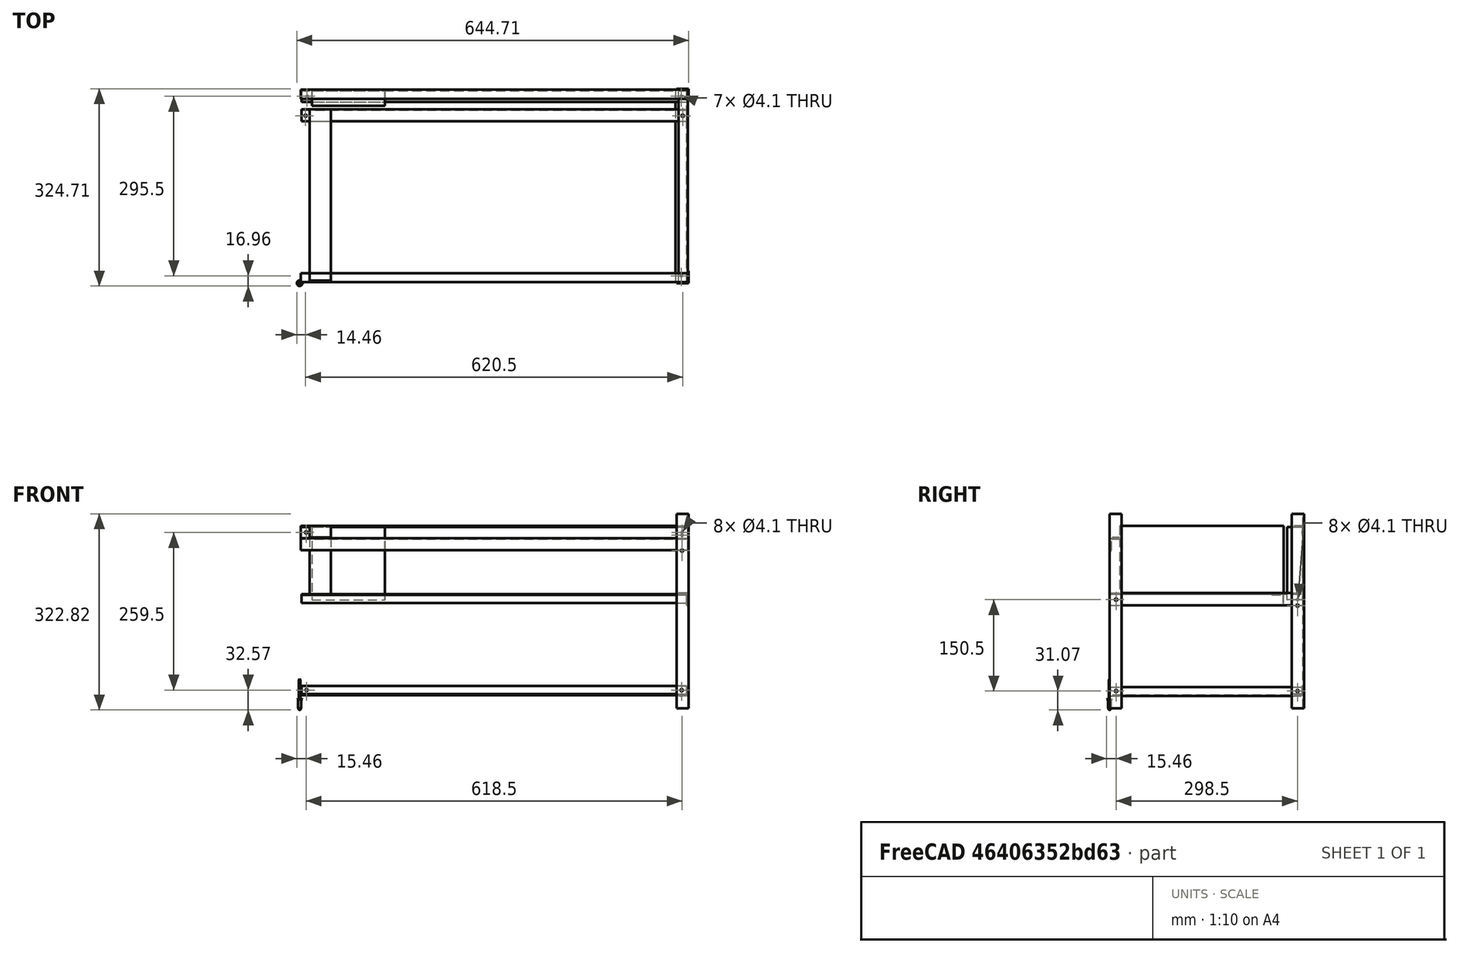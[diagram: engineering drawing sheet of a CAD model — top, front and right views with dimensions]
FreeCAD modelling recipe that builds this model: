
FCSTD DOCUMENT  (FreeCAD 0.17R13541 (Git))
Label: open_air_case_frame
License: All rights reserved
LicenseURL: http://en.wikipedia.org/wiki/All_rights_reserved
objects: TechDraw::DrawViewDimension×88, TechDraw::DrawViewPart×26, Sketcher::SketchObject×18, PartDesign::Hole×14, TechDraw::DrawViewAnnotation×14, TechDraw::DrawProjGroupItem×13, Part::Box×12, TechDraw::DrawSVGTemplate×10, TechDraw::DrawPage×10, PartDesign::FeatureBase×8, PartDesign::Mirrored×8, PartDesign::Body×8, TechDraw::DrawHatch×8, Part::Cut×6, TechDraw::DrawProjGroup×6, Part::Mirroring×5, App::DocumentObjectGroup×5, Part::Extrusion×4, App::FeaturePython×2, Spreadsheet::Sheet×1, +3 more types
note: 98 computed .brp shape members not serialized (recipe doc carries the construction recipe); baked Part::Feature solids carry a one-line shape summary decoded from their .brp

FEATURE [Part::Box] Box  label="Cube"
  AttacherType = Attacher::AttachEngine3D
  Height = 320
  Length = 20
  Width = 20
  expr: Length = Spreadsheet.bar_width
  expr: Width = Spreadsheet.bar_width
  expr: Height = parameters.height
FEATURE [Part::Box] Box001  label="Cut015"
  AttacherType = Attacher::AttachEngine3D
  Height = 320
  Length = 20
  Placement = pos=(1.5,1.5,0) rot=(0,0,1;0rad)
  Width = 20
  expr: Width = Spreadsheet.bar_width
  expr: Length = Spreadsheet.bar_width
  expr: Placement.Base.y = Spreadsheet.bar_thickness
  expr: Height = parameters.height
  expr: Placement.Base.x = Spreadsheet.bar_thickness
FEATURE [Part::Box] Box004  label="Cube002"
  AttacherType = Attacher::AttachEngine3D
  Height = 15
  Length = 20
  Width = 317
  expr: Width = parameters.depth - Spreadsheet.bar_thickness * 2
  expr: Height = Spreadsheet.bar_height
  expr: Length = Spreadsheet.bar_width
FEATURE [Part::Box] Box005  label="Cut016"
  AttacherType = Attacher::AttachEngine3D
  Height = 13.5
  Length = 20
  Placement = pos=(1.5,0,1.5) rot=(0,0,1;0rad)
  Width = 317
  expr: Length = Spreadsheet.bar_width
  expr: Width = parameters.depth - Spreadsheet.bar_thickness * 2
  expr: Placement.Base.z = Spreadsheet.bar_thickness
  expr: Height = Spreadsheet.bar_height - Spreadsheet.bar_thickness
  expr: Placement.Base.x = Spreadsheet.bar_thickness
FEATURE [Part::Box] Box006  label="Cube003"
  AttacherType = Attacher::AttachEngine3D
  Height = 20
  Length = 15
  Width = 317
  expr: Length = Spreadsheet.bar_height
  expr: Width = parameters.depth - Spreadsheet.bar_thickness * 2
  expr: Height = Spreadsheet.bar_width
FEATURE [Part::Box] Box007  label="Cut017"
  AttacherType = Attacher::AttachEngine3D
  Height = 20
  Length = 15
  Placement = pos=(1.5,0,-1.5) rot=(0,0,1;0rad)
  Width = 317
  expr: Placement.Base.z = Spreadsheet.bar_thickness * -1
  expr: Placement.Base.x = Spreadsheet.bar_thickness
  expr: Height = Spreadsheet.bar_width
  expr: Length = Spreadsheet.bar_height
  expr: Width = parameters.depth - Spreadsheet.bar_thickness * 2
FEATURE [Part::Box] Box008  label="Cube004"
  AttacherType = Attacher::AttachEngine3D
  Height = 320
  Length = 20
  Width = 20
  expr: Width = Spreadsheet.bar_width
  expr: Length = Spreadsheet.bar_width
  expr: Height = parameters.height
FEATURE [Part::Box] Box009  label="Cut018"
  AttacherType = Attacher::AttachEngine3D
  Height = 320
  Length = 20
  Placement = pos=(1.5,-1.5,0) rot=(0,0,1;0rad)
  Width = 20
  expr: Width = Spreadsheet.bar_width
  expr: Length = Spreadsheet.bar_width
  expr: Placement.Base.y = Spreadsheet.bar_thickness * -1
  expr: Height = parameters.height
  expr: Placement.Base.x = Spreadsheet.bar_thickness
FEATURE [Part::Box] Box010  label="reference_cube"
  AttacherType = Attacher::AttachEngine3D
  Height = 15
  Length = 634
  Placement = pos=(1.5,0,0) rot=(0,0,1;0rad)
  Width = 20
  expr: Width = Spreadsheet.bar_width
  expr: Length = parameters.width - Spreadsheet.bar_thickness * 4
  expr: Height = Spreadsheet.bar_height
  expr: Placement.Base.x = Spreadsheet.bar_thickness
FEATURE [Part::Box] Box011  label="reference_cube_cut"
  AttacherType = Attacher::AttachEngine3D
  Height = 15
  Length = 634
  Placement = pos=(1.5,1.5,1.5) rot=(0,0,1;0rad)
  Width = 20
  expr: Placement.Base.z = Spreadsheet.bar_thickness
  expr: Placement.Base.y = Spreadsheet.bar_thickness
  expr: Placement.Base.x = Spreadsheet.bar_thickness
  expr: Height = reference_cube.Height
  expr: Width = reference_cube.Width
  expr: Length = reference_cube.Length
FEATURE [Part::Cut] Cut005  label="lower_front_extrude"
  Base = -> Box010
  Placement = pos=(1.5,1.5,23) rot=(0,0,1;0rad)
  Tool = -> Box011
  expr: Placement.Base.z = Spreadsheet.bottom_empty_space + Spreadsheet.bar_thickness * 2
  expr: Placement.Base.y = Spreadsheet.bar_thickness
  expr: Placement.Base.x = Spreadsheet.bar_thickness
FEATURE [Part::Box] Box012  label="Cube007"
  AttacherType = Attacher::AttachEngine3D
  Height = 20
  Length = 637
  Placement = pos=(1.5,0,0) rot=(0,0,1;0rad)
  Width = 15
  expr: Length = parameters.width - Spreadsheet.bar_thickness * 2
  expr: Width = Spreadsheet.bar_height
  expr: Height = Spreadsheet.bar_width
  expr: Placement.Base.x = Spreadsheet.bar_thickness
FEATURE [Part::Box] Box013  label="Cube008"
  AttacherType = Attacher::AttachEngine3D
  Height = 20
  Length = 637
  Placement = pos=(1.5,1.5,-1.5) rot=(0,0,1;0rad)
  Width = 15
  expr: Placement.Base.z = Spreadsheet.bar_thickness * -1
  expr: Placement.Base.y = Spreadsheet.bar_thickness
  expr: Placement.Base.x = Spreadsheet.bar_thickness
  expr: Height = Spreadsheet.bar_width
  expr: Width = Spreadsheet.bar_height
  expr: Length = parameters.width - Spreadsheet.bar_thickness * 2
FEATURE [Part::Cut] Cut004  label="back_left_extrude"
  Base = -> Box008
  Placement = pos=(0,320,0) rot=(0,0,1;0rad)
  Tool = -> Box009
  expr: Placement.Base.y = parameters.depth
FEATURE [Part::Cut] Cut002  label="lower_left_extrude"
  Base = -> Box004
  Placement = pos=(1.5,1.5,21.5) rot=(0,0,1;0rad)
  Tool = -> Box005
  expr: Placement.Base.z = Spreadsheet.bottom_empty_space + Spreadsheet.bar_thickness
  expr: Placement.Base.y = Spreadsheet.bar_thickness
  expr: Placement.Base.x = Spreadsheet.bar_thickness
FEATURE [Part::Cut] Cut001  label="front_left_extrude"
  Base = -> Box
  Tool = -> Box001
FEATURE [Part::Cut] Cut  label="upper_front_extrude"
  Base = -> Box012
  Placement = pos=(0,1.5,250) rot=(0,0,1;0rad)
  Tool = -> Box013
  expr: Placement.Base.y = Spreadsheet.bar_thickness
FEATURE [Part::Cut] Cut013  label="upper_left_extrude"
  Base = -> Box006
  Placement = pos=(1.5,1.5,158) rot=(0,0,1;0rad)
  Tool = -> Box007
  expr: Placement.Base.y = Spreadsheet.bar_thickness
  expr: Placement.Base.x = Spreadsheet.bar_thickness
FEATURE [App::FeaturePython] Dimension  label="width"  # Draft dimension (typed FeaturePython)
  Dimline = (210,-128,0)
  Direction = (0,0,0)
  Distance = 640
  End = (640,0,0)
  Normal = (0,0,1)
  Start = (0,0,0)
FEATURE [App::FeaturePython] Dimension001  label="depth"  # Draft dimension (typed FeaturePython)
  Dimline = (720,145,0)
  Direction = (0,0,0)
  Distance = 320
  End = (640,320,0)
  Normal = (0,0,1)
  Start = (640,0,0)
FEATURE [PartDesign::FeatureBase] BaseFeature
  BaseFeature = -> Cut001
FEATURE [Sketcher::SketchObject] Sketch005
  AttachmentOffset = pos=(0,0,1.5) rot=(0,0,1;0rad)
  ExternalGeometry = -> [BaseFeature]
  MapMode = 5
  Placement = pos=(1.5,0,0) rot=(0.57735,0.57735,0.57735;2.0944rad)
  Support = -> [YZ_Plane]
  expr: Constraints[9] = 4.0999999999999996 / 2
  sketch-geometry (5):
    g0: LineSegment StartX=1.5 StartY=35 StartZ=0 EndX=20 EndY=35 EndZ=0
    g1: LineSegment StartX=20 StartY=35 StartZ=0 EndX=20 EndY=21.5 EndZ=0
    g2: LineSegment StartX=20 StartY=21.5 StartZ=0 EndX=1.5 EndY=21.5 EndZ=0
    g3: LineSegment StartX=1.5 StartY=21.5 StartZ=0 EndX=1.5 EndY=35 EndZ=0
    g4: Circle CenterX=10.75 CenterY=28.25 CenterZ=0 NormalX=0 NormalY=0 NormalZ=1 AngleXU=0 Radius=2.05
  constraints (14):
    c: Coincident(g0,g1)
    c: Coincident(g1,g2)
    c: Coincident(g2,g3)
    c: Coincident(g3,g0)
    c: Horizontal(g0)
    c: Horizontal(g2)
    c: Vertical(g1)
    c: Vertical(g3)
    c: Symmetric(g0,g1,g4)
    c: Radius(g4) = 2.05
    c: PointOnObject(g0,g-3)
    c: DistanceY(g-3,g1) = 21.5
    c: DistanceY(g1,g0) = 13.5
    c: PointOnObject(g0,g-4)
FEATURE [PartDesign::FeatureBase] BaseFeature001
  BaseFeature = -> Cut002
FEATURE [Sketcher::SketchObject] Sketch006
  AttachmentOffset = pos=(0,0,3) rot=(0,0,1;0rad)
  ExternalGeometry = -> [BaseFeature001]
  MapMode = 5
  Placement = pos=(3,0,0) rot=(0.57735,0.57735,0.57735;2.0944rad)
  Support = -> [YZ_Plane001]
  sketch-geometry (8):
    g0: LineSegment StartX=0 StartY=15 StartZ=0 EndX=18.5 EndY=15 EndZ=0
    g1: LineSegment StartX=18.5 StartY=15 StartZ=0 EndX=18.5 EndY=1.5 EndZ=0
    g2: LineSegment StartX=18.5 StartY=1.5 StartZ=0 EndX=0 EndY=1.5 EndZ=0
    g3: LineSegment StartX=0 StartY=1.5 StartZ=0 EndX=0 EndY=15 EndZ=0
    g4: Circle CenterX=9.25 CenterY=8.25 CenterZ=0 NormalX=0 NormalY=0 NormalZ=1 AngleXU=0 Radius=2.05
    g5: GeomPoint X=158.5 Y=15 Z=0
    g6: GeomPoint X=158.5 Y=1.5 Z=0
    g7: LineSegment [constr] StartX=158.5 StartY=15 StartZ=0 EndX=158.5 EndY=1.5 EndZ=0
  constraints (18):
    c: Coincident(g0,g1)
    c: Coincident(g1,g2)
    c: Coincident(g2,g3)
    c: Coincident(g3,g0)
    c: Horizontal(g0)
    c: Horizontal(g2)
    c: Vertical(g1)
    c: Vertical(g3)
    c: Symmetric(g0,g2,g4)
    c: PointOnObject(g0,g-3)
    c: PointOnObject(g1,g-4)
    c: PointOnObject(g0,g-2)
    c: DistanceX(g2,g1) = 18.5
    c: Radius(g4) = 2.05
    c: Symmetric(g0,g-3,g5)
    c: Symmetric(g-4,g2,g6)
    c: Coincident(g7,g5)
    c: Coincident(g7,g6)
FEATURE [PartDesign::Hole] Hole001
  BaseFeature = -> BaseFeature001
  Depth = 24
  DepthType = 1
  Diameter = 4.1
  DrillPoint = 1
  DrillPointAngle = 118
  HoleCutCountersinkAngle = 90
  HoleCutDepth = 0
  HoleCutDiameter = 0
  HoleCutType = 0
  ModelActualThread = false
  Profile = -> Sketch006
  Tapered = false
  TaperedAngle = 90
  ThreadAngle = 0
  ThreadClass = 0
  ThreadCutOffInner = 0
  ThreadCutOffOuter = 0
  ThreadDirection = 0
  ThreadFit = 0
  ThreadPitch = 0
  ThreadSize = 0
  ThreadType = 0
  Threaded = false
FEATURE [PartDesign::FeatureBase] BaseFeature002
  BaseFeature = -> Cut004
FEATURE [Sketcher::SketchObject] Sketch007
  AttachmentOffset = pos=(0,0,1.5) rot=(0,0,1;0rad)
  ExternalGeometry = -> [BaseFeature,BaseFeature002]
  MapMode = 5
  Placement = pos=(1.5,0,0) rot=(0.57735,0.57735,0.57735;2.0944rad)
  Support = -> [YZ_Plane002]
  expr: Constraints[9] = 4.0999999999999996 / 2
  sketch-geometry (10):
    g0: LineSegment StartX=0 StartY=35 StartZ=0 EndX=18.5 EndY=35 EndZ=0
    g1: LineSegment StartX=18.5 StartY=35 StartZ=0 EndX=18.5 EndY=21.5 EndZ=0
    g2: LineSegment StartX=18.5 StartY=21.5 StartZ=0 EndX=0 EndY=21.5 EndZ=0
    g3: LineSegment StartX=0 StartY=21.5 StartZ=0 EndX=0 EndY=35 EndZ=0
    g4: Circle CenterX=9.25 CenterY=28.25 CenterZ=0 NormalX=0 NormalY=0 NormalZ=1 AngleXU=0 Radius=2.05
    g5: Circle CenterX=9.25 CenterY=168.75 CenterZ=0 NormalX=0 NormalY=0 NormalZ=1 AngleXU=0 Radius=2.05
    g6: LineSegment StartX=-2e-11 StartY=178 StartZ=0 EndX=18.5 EndY=178 EndZ=0
    g7: LineSegment StartX=18.5 StartY=178 StartZ=0 EndX=18.5 EndY=159.5 EndZ=0
    g8: LineSegment StartX=18.5 StartY=159.5 StartZ=0 EndX=-2e-11 EndY=159.5 EndZ=0
    g9: LineSegment StartX=-2e-11 StartY=159.5 StartZ=0 EndX=-2e-11 EndY=178 EndZ=0
  constraints (28):
    c: Coincident(g0,g1)
    c: Coincident(g1,g2)
    c: Coincident(g2,g3)
    c: Coincident(g3,g0)
    c: Horizontal(g0)
    c: Horizontal(g2)
    c: Vertical(g1)
    c: Vertical(g3)
    c: Symmetric(g0,g1,g4)
    c: Radius(g4) = 2.05
    c: DistanceY(g-3,g1) = 21.5
    c: DistanceY(g1,g0) = 13.5
    c: PointOnObject(g0,g-4)
    c: PointOnObject(g0,g-2)
    c: Coincident(g6,g7)
    c: Coincident(g7,g8)
    c: Coincident(g8,g9)
    c: Coincident(g9,g6)
    c: Horizontal(g6)
    c: Horizontal(g8)
    c: Vertical(g7)
    c: Vertical(g9)
    c: Symmetric(g6,g7,g5)
    c: PointOnObject(g6,g-5)
    c: PointOnObject(g7,g-4)
    c: Equal(g6,g9)
    c: Radius(g5) = 2.05
    c: DistanceY(g-1,g8) = 159.5
FEATURE [PartDesign::Hole] Hole  label="Front Left Bottom Hole"
  BaseFeature = -> BaseFeature
  Depth = 25
  DepthType = 1
  Diameter = 4.1
  DrillPoint = 1
  DrillPointAngle = 118
  HoleCutCountersinkAngle = 90
  HoleCutDepth = 0
  HoleCutDiameter = 0
  HoleCutType = 0
  ModelActualThread = false
  Profile = -> Sketch005
  Tapered = false
  TaperedAngle = 90
  ThreadAngle = 0
  ThreadClass = 0
  ThreadCutOffInner = 0
  ThreadCutOffOuter = 0
  ThreadDirection = 0
  ThreadFit = 0
  ThreadPitch = 0
  ThreadSize = 0
  ThreadType = 0
  Threaded = false
FEATURE [PartDesign::Hole] Hole002
  BaseFeature = -> BaseFeature002
  Depth = 25
  DepthType = 1
  Diameter = 4.1
  DrillPoint = 1
  DrillPointAngle = 118
  HoleCutCountersinkAngle = 90
  HoleCutDepth = 0
  HoleCutDiameter = 0
  HoleCutType = 0
  ModelActualThread = false
  Profile = -> Sketch007
  Tapered = false
  TaperedAngle = 90
  ThreadAngle = 0
  ThreadClass = 0
  ThreadCutOffInner = 0
  ThreadCutOffOuter = 0
  ThreadDirection = 0
  ThreadFit = 0
  ThreadPitch = 0
  ThreadSize = 0
  ThreadType = 0
  Threaded = false
FEATURE [PartDesign::Mirrored] Mirrored
  BaseFeature = -> Hole001
  MirrorPlane = -> Sketch006 [Axis0]
  Originals = -> [Hole001]
FEATURE [PartDesign::FeatureBase] BaseFeature003
  BaseFeature = -> Cut005
FEATURE [Sketcher::SketchObject] Sketch008  label="Bottom"
  AttachmentOffset = pos=(0,0,1.5) rot=(0,0,1;0rad)
  ExternalGeometry = -> [Mirrored]
  MapMode = 5
  Placement = pos=(0,0,1.5) rot=(0,0,1;0rad)
  Support = -> [XY_Plane001]
  sketch-geometry (8):
    g0: Circle CenterX=10.75 CenterY=10.75 CenterZ=0 NormalX=0 NormalY=0 NormalZ=1 AngleXU=0 Radius=2.05
    g1: LineSegment StartX=1.5 StartY=20 StartZ=0 EndX=20 EndY=20 EndZ=0
    g2: LineSegment StartX=20 StartY=20 StartZ=0 EndX=20 EndY=1.5 EndZ=0
    g3: LineSegment StartX=20 StartY=1.5 StartZ=0 EndX=1.5 EndY=1.5 EndZ=0
    g4: LineSegment StartX=1.5 StartY=1.5 StartZ=0 EndX=1.5 EndY=20 EndZ=0
    g5: GeomPoint X=20 Y=158.5 Z=0
    g6: GeomPoint X=1.5 Y=158.5 Z=0
    g7: LineSegment [constr] StartX=20 StartY=158.5 StartZ=0 EndX=1.5 EndY=158.5 EndZ=0
  constraints (17):
    c: Coincident(g1,g2)
    c: Coincident(g2,g3)
    c: Coincident(g3,g4)
    c: Coincident(g4,g1)
    c: Horizontal(g1)
    c: Horizontal(g3)
    c: Vertical(g2)
    c: Vertical(g4)
    c: Symmetric(g1,g3,g0)
    c: Symmetric(g2,g1,g0)
    c: DistanceY(g-1,g2) = 1.5
    c: DistanceY(g2,g1) = 18.5
    c: Radius(g0) = 2.05
    c: Coincident(g7,g5)
    c: Coincident(g7,g6)
    c: Symmetric(g-4,g-4,g5)
    c: Symmetric(g-3,g-3,g6)
FEATURE [PartDesign::Hole] Hole003
  BaseFeature = -> Mirrored
  Depth = 25
  DepthType = 1
  Diameter = 4.1
  DrillPoint = 1
  DrillPointAngle = 118
  HoleCutCountersinkAngle = 90
  HoleCutDepth = 0
  HoleCutDiameter = 0
  HoleCutType = 0
  ModelActualThread = false
  Profile = -> Sketch008
  Tapered = false
  TaperedAngle = 90
  ThreadAngle = 0
  ThreadClass = 0
  ThreadCutOffInner = 0
  ThreadCutOffOuter = 0
  ThreadDirection = 0
  ThreadFit = 0
  ThreadPitch = 0
  ThreadSize = 0
  ThreadType = 0
  Threaded = false
FEATURE [PartDesign::Mirrored] Mirrored001
  BaseFeature = -> Hole003
  MirrorPlane = -> Sketch008 [Axis0]
  Originals = -> [Hole003]
FEATURE [PartDesign::Body] Body001  label="side_bottom_body"
  BaseFeature = -> Cut002
  Group = -> [BaseFeature001,Sketch006,Hole001,Mirrored,Sketch008,Hole003,Mirrored001]
  Origin = -> Origin001
  Placement = pos=(1.5,1.5,20) rot=(0,0,1;0rad)
  Tip = -> Mirrored001
  expr: Placement.Base.z = Spreadsheet.bar_width
  expr: Placement.Base.y = Spreadsheet.bar_thickness
  expr: Placement.Base.x = Spreadsheet.bar_thickness
FEATURE [Sketcher::SketchObject] Sketch009
  AttachmentOffset = pos=(0,0,1.5) rot=(0,0,1;0rad)
  ExternalGeometry = -> [BaseFeature003]
  MapMode = 5
  Placement = pos=(0,0,1.5) rot=(0,0,1;0rad)
  Support = -> [XY_Plane003]
  sketch-geometry (8):
    g0: Circle CenterX=10.75 CenterY=10.75 CenterZ=0 NormalX=0 NormalY=0 NormalZ=1 AngleXU=0 Radius=2.05
    g1: LineSegment StartX=1.5 StartY=20 StartZ=0 EndX=20 EndY=20 EndZ=0
    g2: LineSegment StartX=20 StartY=20 StartZ=0 EndX=20 EndY=1.5 EndZ=0
    g3: LineSegment StartX=20 StartY=1.5 StartZ=0 EndX=1.5 EndY=1.5 EndZ=0
    g4: LineSegment StartX=1.5 StartY=1.5 StartZ=0 EndX=1.5 EndY=20 EndZ=0
    g5: GeomPoint X=318.5 Y=20 Z=0
    g6: GeomPoint X=318.5 Y=0.75 Z=0
    g7: LineSegment [constr] StartX=318.5 StartY=20 StartZ=0 EndX=318.5 EndY=0.75 EndZ=0
  constraints (19):
    c: Coincident(g1,g2)
    c: Coincident(g2,g3)
    c: Coincident(g3,g4)
    c: Coincident(g4,g1)
    c: Horizontal(g1)
    c: Horizontal(g3)
    c: Vertical(g2)
    c: Vertical(g4)
    c: Symmetric(g1,g3,g0)
    c: Symmetric(g1,g2,g0)
    c: PointOnObject(g1,g-3)
    c: PointOnObject(g3,g-4)
    c: DistanceX(g-1,g3) = 1.5
    c: DistanceX(g3,g2) = 18.5
    c: Radius(g0) = 2.05
    c: Symmetric(g-3,g1,g5)
    c: Coincident(g7,g5)
    c: Coincident(g7,g6)
    c: Symmetric(g-5,g3,g6)
FEATURE [PartDesign::Hole] Hole004
  BaseFeature = -> BaseFeature003
  Depth = 25
  DepthType = 1
  Diameter = 4.1
  DrillPoint = 1
  DrillPointAngle = 118
  HoleCutCountersinkAngle = 90
  HoleCutDepth = 0
  HoleCutDiameter = 0
  HoleCutType = 0
  ModelActualThread = false
  Profile = -> Sketch009
  Tapered = false
  TaperedAngle = 90
  ThreadAngle = 0
  ThreadClass = 0
  ThreadCutOffInner = 0
  ThreadCutOffOuter = 0
  ThreadDirection = 0
  ThreadFit = 0
  ThreadPitch = 0
  ThreadSize = 0
  ThreadType = 0
  Threaded = false
FEATURE [PartDesign::Mirrored] Mirrored002
  BaseFeature = -> Hole004
  MirrorPlane = -> Sketch009 [Axis0]
  Originals = -> [Hole004]
FEATURE [PartDesign::FeatureBase] BaseFeature004
  BaseFeature = -> Cut013
FEATURE [Sketcher::SketchObject] Sketch010
  AttachmentOffset = pos=(0,0,1.5) rot=(0,0,1;0rad)
  ExternalGeometry = -> [BaseFeature004]
  MapMode = 5
  Placement = pos=(1.5,0,0) rot=(0.57735,0.57735,0.57735;2.0944rad)
  Support = -> [YZ_Plane004]
  sketch-geometry (8):
    g0: Circle CenterX=9.25 CenterY=9.25 CenterZ=0 NormalX=0 NormalY=0 NormalZ=1 AngleXU=0 Radius=2.22807
    g1: LineSegment StartX=0 StartY=18.5 StartZ=0 EndX=18.5 EndY=18.5 EndZ=0
    g2: LineSegment StartX=18.5 StartY=18.5 StartZ=0 EndX=18.5 EndY=0 EndZ=0
    g3: LineSegment StartX=18.5 StartY=0 StartZ=0 EndX=0 EndY=0 EndZ=0
    g4: LineSegment StartX=0 StartY=0 StartZ=0 EndX=0 EndY=18.5 EndZ=0
    g5: GeomPoint X=158.5 Y=18.5 Z=0
    g6: GeomPoint X=158.5 Y=0 Z=0
    g7: LineSegment [constr] StartX=158.5 StartY=18.5 StartZ=0 EndX=158.5 EndY=0 EndZ=0
  constraints (18):
    c: Coincident(g1,g2)
    c: Coincident(g2,g3)
    c: Coincident(g3,g4)
    c: Coincident(g4,g1)
    c: Horizontal(g1)
    c: Horizontal(g3)
    c: Vertical(g2)
    c: Symmetric(g1,g3,g0)
    c: Symmetric(g1,g2,g0)
    c: PointOnObject(g3,g-2)
    c: PointOnObject(g3,g-1)
    c: DistanceX(g1,g1) = 18.5
    c: DistanceY(g-1,g1) = 18.5
    c: Symmetric(g-3,g-1,g6)
    c: Symmetric(g1,g-4,g5)
    c: Coincident(g7,g5)
    c: Coincident(g7,g6)
    c: Vertical(g7)
FEATURE [PartDesign::Hole] Hole005
  BaseFeature = -> BaseFeature004
  Depth = 25
  DepthType = 1
  Diameter = 4.1
  DrillPoint = 1
  DrillPointAngle = 118
  HoleCutCountersinkAngle = 90
  HoleCutDepth = 0
  HoleCutDiameter = 0
  HoleCutType = 0
  ModelActualThread = false
  Profile = -> Sketch010
  Tapered = false
  TaperedAngle = 90
  ThreadAngle = 0
  ThreadClass = 0
  ThreadCutOffInner = 0
  ThreadCutOffOuter = 0
  ThreadDirection = 0
  ThreadFit = 0
  ThreadPitch = 0
  ThreadSize = 0
  ThreadType = 0
  Threaded = false
FEATURE [PartDesign::Mirrored] Mirrored003
  BaseFeature = -> Hole005
  MirrorPlane = -> Sketch010 [Axis0]
  Originals = -> [Hole005]
FEATURE [Sketcher::SketchObject] Sketch011
  AttachmentOffset = pos=(0,0,1.5) rot=(0,0,1;0rad)
  ExternalGeometry = -> [Hole]
  MapMode = 5
  Placement = pos=(1.5,0,0) rot=(0.57735,0.57735,0.57735;2.0944rad)
  Support = -> [YZ_Plane]
  expr: Constraints[12] = parameters.height - Spreadsheet.top_empty_space - parameters.graphic_card_height
  sketch-geometry (6):
    g0: LineSegment StartX=1.5 StartY=188 StartZ=0 EndX=20 EndY=188 EndZ=0
    g1: LineSegment StartX=20 StartY=188 StartZ=0 EndX=20 EndY=169.5 EndZ=0
    g2: LineSegment StartX=20 StartY=169.5 StartZ=0 EndX=1.5 EndY=169.5 EndZ=0
    g3: LineSegment StartX=1.5 StartY=169.5 StartZ=0 EndX=1.5 EndY=188 EndZ=0
    g4: GeomPoint X=10.75 Y=178.75 Z=0
    g5: Circle CenterX=10.75 CenterY=178.75 CenterZ=0 NormalX=0 NormalY=0 NormalZ=1 AngleXU=0 Radius=2.05
  constraints (15):
    c: Coincident(g0,g1)
    c: Coincident(g1,g2)
    c: Coincident(g2,g3)
    c: Coincident(g3,g0)
    c: Horizontal(g0)
    c: Horizontal(g2)
    c: Vertical(g1)
    c: Vertical(g3)
    c: Symmetric(g0,g2,g4)
    c: PointOnObject(g2,g-3)
    c: PointOnObject(g1,g-4)
    c: DistanceY(g1,g0) = 18.5
    c: DistanceY(g-1,g0) = 188
    c: Radius(g5) = 2.05
    c: Coincident(g5,g4)
FEATURE [PartDesign::Hole] Hole006  label="Front Left Middle Hole"
  BaseFeature = -> Hole
  Depth = 25
  DepthType = 1
  Diameter = 4.1
  DrillPoint = 1
  DrillPointAngle = 118
  HoleCutCountersinkAngle = 90
  HoleCutDepth = 0
  HoleCutDiameter = 0
  HoleCutType = 0
  ModelActualThread = false
  Profile = -> Sketch011
  Tapered = false
  TaperedAngle = 90
  ThreadAngle = 0
  ThreadClass = 0
  ThreadCutOffInner = 0
  ThreadCutOffOuter = 0
  ThreadDirection = 0
  ThreadFit = 0
  ThreadPitch = 0
  ThreadSize = 0
  ThreadType = 0
  Threaded = false
FEATURE [Part::Mirroring] Part__Mirroring001  label="left_bottom_mirror"
  Base = (1.90735e-06,160,27.5)
  Normal = (1,0,-1.19209e-07)
  Placement = pos=(640,0,0) rot=(0,0,1;0rad)
  Source = -> Body001
  expr: Placement.Base.x = parameters.width
FEATURE [PartDesign::FeatureBase] BaseFeature005
  BaseFeature = -> Cut
FEATURE [Sketcher::SketchObject] Sketch012
  AttachmentOffset = pos=(0,0,1.5) rot=(0,0,1;0rad)
  ExternalGeometry = -> [BaseFeature005]
  MapMode = 5
  Placement = pos=(0,-1.5,0) rot=(1,0,0;1.5708rad)
  Support = -> [XZ_Plane005]
  sketch-geometry (8):
    g0: LineSegment StartX=-17 StartY=18.5 StartZ=0 EndX=1.5 EndY=18.5 EndZ=0
    g1: LineSegment StartX=1.5 StartY=18.5 StartZ=0 EndX=1.5 EndY=0 EndZ=0
    g2: LineSegment StartX=1.5 StartY=0 StartZ=0 EndX=-17 EndY=0 EndZ=0
    g3: LineSegment StartX=-17 StartY=0 StartZ=0 EndX=-17 EndY=18.5 EndZ=0
    g4: Circle CenterX=-7.75 CenterY=9.25 CenterZ=0 NormalX=0 NormalY=0 NormalZ=1 AngleXU=0 Radius=2.05
    g5: GeomPoint X=320 Y=19.25 Z=0
    g6: GeomPoint X=320 Y=0 Z=0
    g7: LineSegment [constr] StartX=320 StartY=19.25 StartZ=0 EndX=320 EndY=0 EndZ=0
  constraints (18):
    c: Coincident(g0,g1)
    c: Coincident(g1,g2)
    c: Coincident(g2,g3)
    c: Coincident(g3,g0)
    c: Horizontal(g0)
    c: Horizontal(g2)
    c: Vertical(g1)
    c: Vertical(g3)
    c: Symmetric(g2,g0,g4)
    c: PointOnObject(g0,g-4)
    c: PointOnObject(g2,g-5)
    c: Radius(g4) = 2.05
    c: Symmetric(g-5,g1,g6)
    c: Symmetric(g0,g-3,g5)
    c: Coincident(g7,g5)
    c: Coincident(g7,g6)
    c: PointOnObject(g0,g-6)
    c: Equal(g0,g3)
FEATURE [PartDesign::Hole] Hole007
  BaseFeature = -> BaseFeature005
  Depth = 25
  DepthType = 1
  Diameter = 4.1
  DrillPoint = 1
  DrillPointAngle = 118
  HoleCutCountersinkAngle = 90
  HoleCutDepth = 0
  HoleCutDiameter = 0
  HoleCutType = 0
  ModelActualThread = false
  Profile = -> Sketch012
  Tapered = false
  TaperedAngle = 90
  ThreadAngle = 0
  ThreadClass = 0
  ThreadCutOffInner = 0
  ThreadCutOffOuter = 0
  ThreadDirection = 0
  ThreadFit = 0
  ThreadPitch = 0
  ThreadSize = 0
  ThreadType = 0
  Threaded = false
FEATURE [PartDesign::Mirrored] Mirrored004
  BaseFeature = -> Hole007
  MirrorPlane = -> Sketch012 [Axis0]
  Originals = -> [Hole007]
FEATURE [PartDesign::Body] Body005  label="top_front_body"
  BaseFeature = -> Cut
  Group = -> [BaseFeature005,Sketch012,Hole007,Mirrored004]
  Origin = -> Origin005
  Placement = pos=(0,1.5,260) rot=(0,0,1;0rad)
  Tip = -> Mirrored004
  expr: Placement.Base.z = parameters.height - Spreadsheet.top_empty_space - (parameters.graphic_card_height - parameters.graphic_card_fixation_height) - Spreadsheet.bar_width
  expr: Placement.Base.y = Spreadsheet.bar_thickness
FEATURE [Sketcher::SketchObject] Sketch013
  AttachmentOffset = pos=(0,0,1.5) rot=(0,0,1;0rad)
  ExternalGeometry = -> [Hole006]
  MapMode = 5
  Placement = pos=(0,-1.5,0) rot=(1,0,0;1.5708rad)
  Support = -> [XZ_Plane]
  sketch-geometry (10):
    g0: LineSegment StartX=1.5 StartY=268.5 StartZ=0 EndX=20 EndY=268.5 EndZ=0
    g1: LineSegment StartX=20 StartY=268.5 StartZ=0 EndX=20 EndY=250 EndZ=0
    g2: LineSegment StartX=20 StartY=250 StartZ=0 EndX=1.5 EndY=250 EndZ=0
    g3: LineSegment StartX=1.5 StartY=250 StartZ=0 EndX=1.5 EndY=268.5 EndZ=0
    g4: Circle CenterX=10.75 CenterY=259.25 CenterZ=0 NormalX=0 NormalY=0 NormalZ=1 AngleXU=0 Radius=2.05
    g5: LineSegment StartX=3 StartY=36.5 StartZ=0 EndX=20 EndY=36.5 EndZ=0
    g6: LineSegment StartX=20 StartY=36.5 StartZ=0 EndX=20 EndY=23 EndZ=0
    g7: LineSegment StartX=20 StartY=23 StartZ=0 EndX=3 EndY=23 EndZ=0
    g8: LineSegment StartX=3 StartY=23 StartZ=0 EndX=3 EndY=36.5 EndZ=0
    g9: Circle CenterX=11.5 CenterY=29.75 CenterZ=0 NormalX=0 NormalY=0 NormalZ=1 AngleXU=0 Radius=2.05
  constraints (28):
    c: Coincident(g0,g1)
    c: Coincident(g1,g2)
    c: Coincident(g2,g3)
    c: Coincident(g3,g0)
    c: Horizontal(g0)
    c: Horizontal(g2)
    c: Vertical(g1)
    c: Vertical(g3)
    c: Symmetric(g0,g1,g4)
    c: PointOnObject(g0,g-4)
    c: PointOnObject(g0,g-3)
    c: Equal(g0,g1)
    c: Radius(g4) = 2.05
    c: DistanceY(g-3,g1) = 250
    c: Coincident(g5,g6)
    c: Coincident(g6,g7)
    c: Coincident(g7,g8)
    c: Coincident(g8,g5)
    c: Horizontal(g5)
    c: Horizontal(g7)
    c: Vertical(g6)
    c: Vertical(g8)
    c: Symmetric(g5,g6,g9)
    c: PointOnObject(g5,g-3)
    c: Radius(g9) = 2.05
    c: DistanceY(g-1,g6) = 23
    c: DistanceY(g6,g5) = 13.5
    c: DistanceX(g5,g5) = 17
FEATURE [PartDesign::Hole] Hole008  label="ZX Holes"
  BaseFeature = -> Hole006
  Depth = 25
  DepthType = 1
  Diameter = 4.1
  DrillPoint = 1
  DrillPointAngle = 118
  HoleCutCountersinkAngle = 90
  HoleCutDepth = 0
  HoleCutDiameter = 0
  HoleCutType = 0
  ModelActualThread = false
  Profile = -> Sketch013
  Tapered = false
  TaperedAngle = 90
  ThreadAngle = 0
  ThreadClass = 0
  ThreadCutOffInner = 0
  ThreadCutOffOuter = 0
  ThreadDirection = 0
  ThreadFit = 0
  ThreadPitch = 0
  ThreadSize = 0
  ThreadType = 0
  Threaded = false
FEATURE [PartDesign::Body] Body  label="vertical_front_left_body"
  BaseFeature = -> Cut001
  Group = -> [BaseFeature,Sketch005,Hole,Sketch011,Hole006,Sketch013,Hole008]
  Origin = -> Origin
  Tip = -> Hole008
FEATURE [Part::Mirroring] Part__Mirroring002  label="vertical_front_left_mirror"
  Base = (0,0,0)
  Normal = (1,0,0)
  Placement = pos=(640,0,0) rot=(0,0,1;0rad)
  Source = -> Body
  expr: Placement.Base.x = parameters.width
FEATURE [Sketcher::SketchObject] Sketch  label="cards_holder_sketch"
  Placement = pos=(0,0,0) rot=(0.57735,-0.57735,-0.57735;2.0944rad)
  expr: Constraints[15] = Spreadsheet.bar_thickness
  expr: Constraints[12] = Spreadsheet.bar_width
  expr: Constraints[14] = Spreadsheet.bar_height
  sketch-geometry (6):
    g0: LineSegment StartX=-20 StartY=0 StartZ=0 EndX=-20 EndY=15 EndZ=0
    g1: LineSegment StartX=-20 StartY=15 StartZ=0 EndX=0 EndY=15 EndZ=0
    g2: LineSegment StartX=0 StartY=15 StartZ=0 EndX=0 EndY=13.5 EndZ=0
    g3: LineSegment StartX=0 StartY=13.5 StartZ=0 EndX=-18.5 EndY=13.5 EndZ=0
    g4: LineSegment StartX=-18.5 StartY=13.5 StartZ=0 EndX=-18.5 EndY=0 EndZ=0
    g5: LineSegment StartX=-18.5 StartY=0 StartZ=0 EndX=-20 EndY=0 EndZ=0
  constraints (18):
    c: Coincident(g0,g1)
    c: Horizontal(g1)
    c: Coincident(g1,g2)
    c: Vertical(g2)
    c: Coincident(g2,g3)
    c: Horizontal(g3)
    c: Coincident(g3,g4)
    c: Coincident(g4,g5)
    c: Coincident(g5,g0)
    c: Horizontal(g5)
    c: Parallel(g2,g4)
    c: Parallel(g4,g0)
    c: DistanceX(g0,g1) = 20
    c: Equal(g5,g2)
    c: DistanceY(g0,g0) = 15
    c: DistanceX(g0,g4) = 1.5
    c: PointOnObject(g2,g-2)
    c: PointOnObject(g4,g-1)
FEATURE [Part::Extrusion] Extrude001  label="cards_holder_extrude"
  Base = -> Sketch
  Dir = (-1,0,0)
  DirMode = 2
  FaceMakerClass = Part::FaceMakerBullseye
  LengthFwd = 634
  LengthRev = 0
  Reversed = true
  Solid = true
  Symmetric = false
  expr: LengthFwd = parameters.width - Spreadsheet.bar_thickness * 4
FEATURE [PartDesign::FeatureBase] BaseFeature006
  BaseFeature = -> Extrude001
FEATURE [Sketcher::SketchObject] Sketch014  label="graphic_card_sketch"
  Placement = pos=(16.5,0,0) rot=(0.57735,0.57735,0.57735;2.0944rad)
  expr: Constraints.graphic_card_height = parameters.graphic_card_height
  expr: Constraints.graphic_card_fixation_height = parameters.graphic_card_fixation_height
  expr: Constraints.graphic_card_length = parameters.graphic_card_length
  expr: Placement.Base.x = Spreadsheet.bar_height + Spreadsheet.bar_thickness
  expr: Constraints[21] = parameters.height - Spreadsheet.top_empty_space - (parameters.graphic_card_height - parameters.graphic_card_fixation_height)
  sketch-geometry (11):
    g0: LineSegment StartX=4.5 StartY=281 StartZ=0 EndX=4.5 EndY=280 EndZ=0
    g1: LineSegment StartX=4.5 StartY=280 StartZ=0 EndX=16.5 EndY=280 EndZ=0
    g2: LineSegment StartX=16.5 StartY=280 StartZ=0 EndX=16.5 EndY=188 EndZ=0
    g3: LineSegment StartX=16.5 StartY=188 StartZ=0 EndX=286.5 EndY=188 EndZ=0
    g4: LineSegment StartX=286.5 StartY=188 StartZ=0 EndX=286.5 EndY=300 EndZ=0
    g5: LineSegment StartX=286.5 StartY=300 StartZ=0 EndX=16.5 EndY=300 EndZ=0
    g6: LineSegment StartX=16.5 StartY=300 StartZ=0 EndX=16.5 EndY=281 EndZ=0
    g7: LineSegment StartX=16.5 StartY=281 StartZ=0 EndX=4.5 EndY=281 EndZ=0
    g8: GeomPoint X=291.5 Y=234 Z=0
    g9: GeomPoint X=286.5 Y=244 Z=0
    g10: LineSegment [constr] StartX=16.5 StartY=300 StartZ=0 EndX=16.5 EndY=320 EndZ=0
  constraints (28):
    c: Vertical(g0)
    c: Coincident(g0,g1)
    c: Coincident(g1,g2)
    c: Horizontal(g3)
    c: Coincident(g3,g4)
    c: Vertical(g4)
    c: Coincident(g4,g5)
    c: Horizontal(g5)
    c: Coincident(g5,g6)
    c: Coincident(g6,g7)
    c: Coincident(g7,g0)
    c: DistanceY(g0,g0) = 1
    c: PointOnObject(g6,g2)
    c: DistanceX(g5,g4) = 270  'graphic_card_length'
    c: DistanceY(g3,g0) = 92  'graphic_card_fixation_height'
    c: DistanceY(g3,g4) = 112  'graphic_card_height'
    c: DistanceX(g0,g6) = 12
    c: Parallel(g6,g0)
    c: Parallel(g3,g7)
    c: Parallel(g7,g1)
    c: DistanceX(g-1,g5) = 16.5
    c: DistanceY(g-1,g0) = 280
    c: Symmetric(g4,g3,g9)
    c: Coincident(g10,g5)
    c: Vertical(g10)
    c: Perpendicular(g2,g3)
    c: PointOnObject(g3,g2)
    c: Coincident(g2,g3)
FEATURE [Sketcher::SketchObject] Sketch015  label="fans_bar_sketch"
  Placement = pos=(0,0,0) rot=(0.57735,-0.57735,-0.57735;2.0944rad)
  expr: Constraints.thickness = Spreadsheet.bar_thickness
  expr: Constraints.height = Spreadsheet.bar_height
  expr: Constraints.width = Spreadsheet.bar_width
  sketch-geometry (6):
    g0: LineSegment StartX=-15 StartY=0 StartZ=0 EndX=-15 EndY=20 EndZ=0
    g1: LineSegment StartX=-15 StartY=20 StartZ=0 EndX=0 EndY=20 EndZ=0
    g2: LineSegment StartX=0 StartY=20 StartZ=0 EndX=0 EndY=18.5 EndZ=0
    g3: LineSegment StartX=0 StartY=18.5 StartZ=0 EndX=-13.5 EndY=18.5 EndZ=0
    g4: LineSegment StartX=-13.5 StartY=18.5 StartZ=0 EndX=-13.5 EndY=0 EndZ=0
    g5: LineSegment StartX=-13.5 StartY=0 StartZ=0 EndX=-15 EndY=0 EndZ=0
  constraints (18):
    c: Coincident(g0,g1)
    c: Horizontal(g1)
    c: Coincident(g1,g2)
    c: Vertical(g2)
    c: Coincident(g2,g3)
    c: Horizontal(g3)
    c: Coincident(g3,g4)
    c: Coincident(g4,g5)
    c: Coincident(g5,g0)
    c: Horizontal(g5)
    c: Parallel(g2,g4)
    c: Parallel(g4,g0)
    c: DistanceX(g0,g1) = 15  'height'
    c: Equal(g5,g2)
    c: DistanceY(g0,g0) = 20  'width'
    c: DistanceX(g0,g4) = 1.5  'thickness'
    c: PointOnObject(g2,g-2)
    c: PointOnObject(g4,g-1)
FEATURE [Part::Extrusion] Extrude002  label="fans_bar_extrude"
  Base = -> Sketch015
  Dir = (-1,0,0)
  DirMode = 2
  FaceMakerClass = Part::FaceMakerBullseye
  LengthFwd = 637
  LengthRev = 0
  Reversed = true
  Solid = true
  Symmetric = false
  expr: LengthFwd = parameters.width - Spreadsheet.bar_thickness * 2
FEATURE [App::DocumentObjectGroup] Group002  label="extrudes"
  Group = -> [Cut005,Cut004,Cut002,Cut001,Cut,Cut013,Extrude001,Extrude002]
FEATURE [PartDesign::FeatureBase] BaseFeature007
  BaseFeature = -> Extrude002
FEATURE [Sketcher::SketchObject] Sketch016
  AttachmentOffset = pos=(0,0,-13.5) rot=(0,0,1;0rad)
  ExternalGeometry = -> [BaseFeature007]
  MapMode = 5
  Placement = pos=(0,13.5,1e-12) rot=(1,0,0;1.5708rad)
  Support = -> [XZ_Plane007]
  sketch-geometry (6):
    g0: Circle CenterX=9.25 CenterY=9.25 CenterZ=0 NormalX=0 NormalY=0 NormalZ=1 AngleXU=0 Radius=2.05
    g1: LineSegment StartX=0 StartY=18.5 StartZ=0 EndX=18.5 EndY=18.5 EndZ=0
    g2: LineSegment StartX=18.5 StartY=18.5 StartZ=0 EndX=18.5 EndY=0 EndZ=0
    g3: LineSegment StartX=18.5 StartY=0 StartZ=0 EndX=0 EndY=0 EndZ=0
    g4: LineSegment StartX=0 StartY=0 StartZ=0 EndX=0 EndY=18.5 EndZ=0
    g5: LineSegment [constr] StartX=318.5 StartY=18.5 StartZ=0 EndX=318.5 EndY=0 EndZ=0
  constraints (17):
    c: Coincident(g1,g2)
    c: Coincident(g2,g3)
    c: Coincident(g3,g4)
    c: Coincident(g4,g1)
    c: Horizontal(g1)
    c: Horizontal(g3)
    c: Vertical(g2)
    c: Vertical(g4)
    c: Symmetric(g2,g1,g0)
    c: PointOnObject(g1,g-3)
    c: PointOnObject(g3,g-4)
    c: Equal(g1,g2)
    c: Radius(g0) = 2.05
    c: Coincident(g-3,g1)
    c: Vertical(g5)
    c: Symmetric(g-3,g1,g5)
    c: Symmetric(g-4,g-1,g5)
FEATURE [PartDesign::Hole] Hole009
  BaseFeature = -> BaseFeature007
  Depth = 25
  DepthType = 1
  Diameter = 4.1
  DrillPoint = 1
  DrillPointAngle = 118
  HoleCutCountersinkAngle = 90
  HoleCutDepth = 0
  HoleCutDiameter = 0
  HoleCutType = 0
  ModelActualThread = false
  Profile = -> Sketch016
  Tapered = false
  TaperedAngle = 90
  ThreadAngle = 0
  ThreadClass = 0
  ThreadCutOffInner = 0
  ThreadCutOffOuter = 0
  ThreadDirection = 0
  ThreadFit = 0
  ThreadPitch = 0
  ThreadSize = 0
  ThreadType = 0
  Threaded = false
FEATURE [PartDesign::Mirrored] Mirrored005
  BaseFeature = -> Hole009
  MirrorPlane = -> Sketch016 [Axis0]
  Originals = -> [Hole009]
FEATURE [PartDesign::Body] Body007  label="fans_bar_body"
  BaseFeature = -> Extrude002
  Group = -> [BaseFeature007,Sketch016,Hole009,Mirrored005]
  Origin = -> Origin007
  Placement = pos=(1.5,303.5,280) rot=(0,0,1;0rad)
  Tip = -> Mirrored005
  expr: Placement.Base.z = parameters.height - Spreadsheet.top_empty_space - Spreadsheet.bar_width
  expr: Placement.Base.y = parameters.depth - Spreadsheet.bar_height - Spreadsheet.bar_thickness
  expr: Placement.Base.x = Spreadsheet.bar_thickness
FEATURE [Sketcher::SketchObject] Sketch017
  AttachmentOffset = pos=(0,0,-18.5) rot=(0,0,1;0rad)
  ExternalGeometry = -> [Hole002]
  MapMode = 5
  Placement = pos=(0,18.5,2e-12) rot=(1,0,0;1.5708rad)
  Support = -> [XZ_Plane002]
  sketch-geometry (10):
    g0: Circle CenterX=10.75 CenterY=284.75 CenterZ=0 NormalX=0 NormalY=0 NormalZ=1 AngleXU=0 Radius=2.05
    g1: LineSegment StartX=1.5 StartY=294 StartZ=0 EndX=20 EndY=294 EndZ=0
    g2: LineSegment StartX=20 StartY=294 StartZ=0 EndX=20 EndY=275.5 EndZ=0
    g3: LineSegment StartX=20 StartY=275.5 StartZ=0 EndX=1.5 EndY=275.5 EndZ=0
    g4: LineSegment StartX=1.5 StartY=275.5 StartZ=0 EndX=1.5 EndY=294 EndZ=0
    g5: Circle CenterX=11.5 CenterY=29.75 CenterZ=0 NormalX=0 NormalY=0 NormalZ=1 AngleXU=0 Radius=2.05
    g6: LineSegment StartX=3 StartY=36.5 StartZ=0 EndX=20 EndY=36.5 EndZ=0
    g7: LineSegment StartX=20 StartY=36.5 StartZ=0 EndX=20 EndY=23 EndZ=0
    g8: LineSegment StartX=20 StartY=23 StartZ=0 EndX=3 EndY=23 EndZ=0
    g9: LineSegment StartX=3 StartY=23 StartZ=0 EndX=3 EndY=36.5 EndZ=0
  constraints (28):
    c: Coincident(g1,g2)
    c: Coincident(g2,g3)
    c: Coincident(g3,g4)
    c: Coincident(g4,g1)
    c: Horizontal(g1)
    c: Horizontal(g3)
    c: Vertical(g2)
    c: Vertical(g4)
    c: Symmetric(g1,g2,g0)
    c: PointOnObject(g1,g-3)
    c: PointOnObject(g1,g-4)
    c: Equal(g2,g1)
    c: DistanceY(g-4,g3) = 275.5
    c: Radius(g0) = 2.05
    c: Coincident(g6,g7)
    c: Coincident(g7,g8)
    c: Coincident(g8,g9)
    c: Coincident(g9,g6)
    c: Horizontal(g6)
    c: Horizontal(g8)
    c: Vertical(g7)
    c: Vertical(g9)
    c: Symmetric(g6,g7,g5)
    c: PointOnObject(g7,g-3)
    c: DistanceY(g7,g6) = 13.5
    c: DistanceX(g6,g6) = 17
    c: DistanceY(g-3,g7) = 23
    c: Radius(g5) = 2.05
FEATURE [PartDesign::Hole] Hole010
  BaseFeature = -> Hole002
  Depth = 25
  DepthType = 1
  Diameter = 4.1
  DrillPoint = 1
  DrillPointAngle = 118
  HoleCutCountersinkAngle = 90
  HoleCutDepth = 0
  HoleCutDiameter = 0
  HoleCutType = 0
  ModelActualThread = false
  Profile = -> Sketch017
  Tapered = false
  TaperedAngle = 90
  ThreadAngle = 0
  ThreadClass = 0
  ThreadCutOffInner = 0
  ThreadCutOffOuter = 0
  ThreadDirection = 0
  ThreadFit = 0
  ThreadPitch = 0
  ThreadSize = 0
  ThreadType = 0
  Threaded = false
FEATURE [PartDesign::Body] Body002  label="vertical_back_body"
  BaseFeature = -> Cut004
  Group = -> [BaseFeature002,Sketch007,Hole002,Sketch017,Hole010]
  Origin = -> Origin002
  Placement = pos=(0,300,0) rot=(0,0,1;0rad)
  Tip = -> Hole010
  expr: Placement.Base.y = parameters.depth - Spreadsheet.bar_width
FEATURE [Part::Mirroring] Part__Mirroring  label="vertical_back_left_mirror"
  Base = (1.52588e-05,310,160)
  Normal = (1,0,-1.19209e-07)
  Placement = pos=(640,0,0) rot=(0,0,1;0rad)
  Source = -> Body002
  expr: Placement.Base.x = parameters.width
FEATURE [Sketcher::SketchObject] Sketch018
  ExternalGeometry = -> [Mirrored002]
  MapMode = 5
  Placement = pos=(0,0,0) rot=(1,0,0;1.5708rad)
  Support = -> [XZ_Plane003]
  sketch-geometry (6):
    g0: Circle CenterX=10 CenterY=8.25 CenterZ=0 NormalX=0 NormalY=0 NormalZ=1 AngleXU=0 Radius=2.05
    g1: LineSegment StartX=1.5 StartY=15 StartZ=0 EndX=18.5 EndY=15 EndZ=0
    g2: LineSegment StartX=18.5 StartY=15 StartZ=0 EndX=18.5 EndY=1.5 EndZ=0
    g3: LineSegment StartX=18.5 StartY=1.5 StartZ=0 EndX=1.5 EndY=1.5 EndZ=0
    g4: LineSegment StartX=1.5 StartY=1.5 StartZ=0 EndX=1.5 EndY=15 EndZ=0
    g5: LineSegment [constr] StartX=318.5 StartY=15 StartZ=0 EndX=318.5 EndY=1.5 EndZ=0
  constraints (16):
    c: Coincident(g1,g2)
    c: Coincident(g2,g3)
    c: Coincident(g3,g4)
    c: Coincident(g4,g1)
    c: Horizontal(g1)
    c: Horizontal(g3)
    c: Vertical(g2)
    c: Vertical(g4)
    c: Symmetric(g1,g2,g0)
    c: PointOnObject(g1,g-4)
    c: PointOnObject(g1,g-5)
    c: PointOnObject(g3,g-3)
    c: DistanceX(g1,g1) = 17
    c: Radius(g0) = 2.05
    c: Symmetric(g-4,g1,g5)
    c: Symmetric(g-3,g3,g5)
FEATURE [PartDesign::Hole] Hole011
  BaseFeature = -> Mirrored002
  Depth = 25
  DepthType = 1
  Diameter = 4.1
  DrillPoint = 1
  DrillPointAngle = 118
  HoleCutCountersinkAngle = 90
  HoleCutDepth = 0
  HoleCutDiameter = 0
  HoleCutType = 0
  ModelActualThread = false
  Profile = -> Sketch018
  Tapered = false
  TaperedAngle = 90
  ThreadAngle = 0
  ThreadClass = 0
  ThreadCutOffInner = 0
  ThreadCutOffOuter = 0
  ThreadDirection = 0
  ThreadFit = 0
  ThreadPitch = 0
  ThreadSize = 0
  ThreadType = 0
  Threaded = false
FEATURE [PartDesign::Mirrored] Mirrored006
  BaseFeature = -> Hole011
  MirrorPlane = -> Sketch018 [Axis0]
  Originals = -> [Hole011]
FEATURE [PartDesign::Body] Body003  label="bottom_body"
  BaseFeature = -> Cut005
  Group = -> [BaseFeature003,Sketch009,Hole004,Mirrored002,Sketch018,Hole011,Mirrored006]
  Origin = -> Origin003
  Placement = pos=(1.5,1.5,21.5) rot=(0,0,1;0rad)
  Tip = -> Mirrored006
  expr: Placement.Base.z = Spreadsheet.bottom_empty_space + Spreadsheet.bar_thickness
  expr: Placement.Base.y = Spreadsheet.bar_thickness
  expr: Placement.Base.x = Spreadsheet.bar_thickness
FEATURE [Part::Mirroring] Part__Mirroring004  label="front_bottom_mirror"
  Base = (490,3.8147e-06,29)
  Normal = (0,1,-1.19209e-07)
  Placement = pos=(0,320,0) rot=(0,0,1;0rad)
  Source = -> Body003
  expr: Placement.Base.y = parameters.depth
FEATURE [Sketcher::SketchObject] Sketch019
  AttachmentOffset = pos=(0,0,20) rot=(0,0,1;0rad)
  ExternalGeometry = -> [Mirrored003]
  MapMode = 5
  Placement = pos=(0,0,20) rot=(0,0,1;0rad)
  Support = -> [XY_Plane004]
  sketch-geometry (5):
    g0: Circle CenterX=8.25 CenterY=274.25 CenterZ=0 NormalX=0 NormalY=0 NormalZ=1 AngleXU=0 Radius=2.05
    g1: LineSegment StartX=1.5 StartY=283.5 StartZ=0 EndX=15 EndY=283.5 EndZ=0
    g2: LineSegment StartX=15 StartY=283.5 StartZ=0 EndX=15 EndY=265 EndZ=0
    g3: LineSegment StartX=15 StartY=265 StartZ=0 EndX=1.5 EndY=265 EndZ=0
    g4: LineSegment StartX=1.5 StartY=265 StartZ=0 EndX=1.5 EndY=283.5 EndZ=0
  constraints (14):
    c: Coincident(g1,g2)
    c: Coincident(g2,g3)
    c: Coincident(g3,g4)
    c: Coincident(g4,g1)
    c: Horizontal(g1)
    c: Horizontal(g3)
    c: Vertical(g2)
    c: Vertical(g4)
    c: Symmetric(g1,g2,g0)
    c: PointOnObject(g1,g-4)
    c: PointOnObject(g2,g-3)
    c: Radius(g0) = 2.05
    c: DistanceY(g2,g1) = 18.5
    c: DistanceY(g-4,g3) = 265
FEATURE [PartDesign::Hole] Hole012
  BaseFeature = -> Mirrored003
  Depth = 25
  DepthType = 1
  Diameter = 4.1
  DrillPoint = 1
  DrillPointAngle = 118
  HoleCutCountersinkAngle = 90
  HoleCutDepth = 0
  HoleCutDiameter = 0
  HoleCutType = 0
  ModelActualThread = false
  Profile = -> Sketch019
  Tapered = false
  TaperedAngle = 90
  ThreadAngle = 0
  ThreadClass = 0
  ThreadCutOffInner = 0
  ThreadCutOffOuter = 0
  ThreadDirection = 0
  ThreadFit = 0
  ThreadPitch = 0
  ThreadSize = 0
  ThreadType = 0
  Threaded = false
FEATURE [PartDesign::Body] Body004  label="side_middle_body"
  BaseFeature = -> Cut013
  Group = -> [BaseFeature004,Sketch010,Hole005,Mirrored003,Sketch019,Hole012]
  Origin = -> Origin004
  Placement = pos=(1.5,1.5,169.5) rot=(0,0,1;0rad)
  Tip = -> Hole012
  expr: Placement.Base.z = parameters.height - Spreadsheet.top_empty_space - parameters.graphic_card_height - Spreadsheet.bar_width + Spreadsheet.bar_thickness
  expr: Placement.Base.y = Spreadsheet.bar_thickness
  expr: Placement.Base.x = Spreadsheet.bar_thickness
FEATURE [Part::Mirroring] Part__Mirroring003  label="left_middle_mirror"
  Base = (1.52588e-05,160,169.5)
  Normal = (1,0,-1.19209e-07)
  Placement = pos=(640,0,0) rot=(0,0,1;0rad)
  Source = -> Body004
  expr: Placement.Base.x = parameters.width
FEATURE [App::DocumentObjectGroup] Group001  label="mirrors"
  Group = -> [Part__Mirroring003,Part__Mirroring002,Part__Mirroring001,Part__Mirroring004,Part__Mirroring]
FEATURE [Sketcher::SketchObject] Sketch020
  AttachmentOffset = pos=(0,0,15) rot=(0,0,1;0rad)
  ExternalGeometry = -> [BaseFeature006]
  MapMode = 5
  Placement = pos=(0,0,15) rot=(0,0,1;0rad)
  Support = -> [XY_Plane006]
  sketch-geometry (6):
    g0: Circle CenterX=6.75 CenterY=9.25 CenterZ=0 NormalX=0 NormalY=0 NormalZ=1 AngleXU=0 Radius=2.05
    g1: LineSegment StartX=0 StartY=18.5 StartZ=0 EndX=13.5 EndY=18.5 EndZ=0
    g2: LineSegment StartX=13.5 StartY=18.5 StartZ=0 EndX=13.5 EndY=0 EndZ=0
    g3: LineSegment StartX=13.5 StartY=0 StartZ=0 EndX=0 EndY=0 EndZ=0
    g4: LineSegment StartX=0 StartY=0 StartZ=0 EndX=0 EndY=18.5 EndZ=0
    g5: LineSegment [constr] StartX=317 StartY=18.5 StartZ=0 EndX=317 EndY=0 EndZ=0
  constraints (17):
    c: Coincident(g1,g2)
    c: Coincident(g2,g3)
    c: Coincident(g3,g4)
    c: Coincident(g4,g1)
    c: Horizontal(g1)
    c: Horizontal(g3)
    c: Vertical(g2)
    c: Vertical(g4)
    c: PointOnObject(g1,g-2)
    c: Symmetric(g1,g2,g0)
    c: Radius(g0) = 2.05
    c: PointOnObject(g1,g-3)
    c: PointOnObject(g3,g-4)
    c: DistanceX(g-1,g2) = 13.5
    c: Vertical(g5)
    c: Symmetric(g1,g-3,g5)
    c: Symmetric(g-1,g-4,g5)
FEATURE [PartDesign::Hole] Hole013
  BaseFeature = -> BaseFeature006
  Depth = 25
  DepthType = 1
  Diameter = 4.1
  DrillPoint = 1
  DrillPointAngle = 118
  HoleCutCountersinkAngle = 90
  HoleCutDepth = 0
  HoleCutDiameter = 0
  HoleCutType = 0
  ModelActualThread = false
  Profile = -> Sketch020
  Tapered = false
  TaperedAngle = 90
  ThreadAngle = 0
  ThreadClass = 0
  ThreadCutOffInner = 0
  ThreadCutOffOuter = 0
  ThreadDirection = 0
  ThreadFit = 0
  ThreadPitch = 0
  ThreadSize = 0
  ThreadType = 0
  Threaded = false
FEATURE [PartDesign::Mirrored] Mirrored007
  BaseFeature = -> Hole013
  MirrorPlane = -> Sketch020 [Axis0]
  Originals = -> [Hole013]
FEATURE [PartDesign::Body] Body006  label="cards_holder_body"
  BaseFeature = -> Extrude001
  Group = -> [BaseFeature006,Sketch020,Hole013,Mirrored007]
  Origin = -> Origin006
  Placement = pos=(3,266.5,173) rot=(0,0,1;0rad)
  Tip = -> Mirrored007
  expr: Placement.Base.z = parameters.height - Spreadsheet.top_empty_space - parameters.graphic_card_height - Spreadsheet.bar_height
  expr: Placement.Base.x = Spreadsheet.bar_thickness * 2
  expr: Placement.Base.y = Spreadsheet.bar_height + Spreadsheet.bar_thickness + parameters.graphic_card_length - Spreadsheet.bar_width
FEATURE [App::DocumentObjectGroup] Group  label="frame"
  Group = -> [Body,Body001,Body002,Body004,Body003,Body005,Body006,Body007,Group001]
FEATURE [Spreadsheet::Sheet] Spreadsheet  label="parameters"
  cells = A1=Angle bar thickness; B1(bar_thickness)==1.5mm; E1=Angle bar raw material required; A2=Angle bar width; B2(bar_width)==20mm; E2=Width; F2=Height; G2=Thickness; H2=Length required; A3=Angle bar height; B3(bar_height)==15mm; E3==parameters.bar_height; F3==parameters.bar_width; H3==parameters.width * 5 + parameters.depth * 4; A4=Graphic card body length; B4(graphic_card_length)==270mm; E4==parameters.bar_width; F4==parameters.bar_width; H4==parameters.height * 4; A5=Graphic card body height; B5(graphic_card_height)==112mm; A6=Graphic card fixation height; B6(graphic_card_fixation_height)==92mm; A7=Case width; B7(width)==640mm; A8=Case height; B8(height)==320mm; A9=Case depth; B9(depth)==320mm; A10=Case bottom empty space; B10(bottom_empty_space)==20mm; A11=Case top empty space; B11(top_empty_space)==20mm
FEATURE [Part::Extrusion] Extrude  label="graphic_card_extrude"
  Base = -> Sketch014
  Dir = (1,0,0)
  DirMode = 2
  FaceMakerClass = Part::FaceMakerBullseye
  LengthFwd = 35
  LengthRev = 0
  Solid = true
  Symmetric = false
FEATURE [Sketcher::SketchObject] Sketch022  label="fan_sketch"
  Placement = pos=(20,0,0) rot=(0.57735,0.57735,0.57735;2.0944rad)
  expr: Constraints[11] = parameters.height - Spreadsheet.top_empty_space - Spreadsheet.bar_thickness
  expr: Constraints[10] = parameters.depth - 2 * Spreadsheet.bar_thickness
  expr: Placement.Base.x = Spreadsheet.bar_width
  sketch-geometry (4):
    g0: LineSegment StartX=292 StartY=298.5 StartZ=0 EndX=317 EndY=298.5 EndZ=0
    g1: LineSegment StartX=317 StartY=298.5 StartZ=0 EndX=317 EndY=178.5 EndZ=0
    g2: LineSegment StartX=317 StartY=178.5 StartZ=0 EndX=292 EndY=178.5 EndZ=0
    g3: LineSegment StartX=292 StartY=178.5 StartZ=0 EndX=292 EndY=298.5 EndZ=0
  constraints (12):
    c: Coincident(g0,g1)
    c: Coincident(g1,g2)
    c: Coincident(g2,g3)
    c: Coincident(g3,g0)
    c: Horizontal(g0)
    c: Horizontal(g2)
    c: Vertical(g1)
    c: Vertical(g3)
    c: DistanceX(g2,g1) = 25  'depth'
    c: DistanceY(g1,g0) = 120  'size'
    c: DistanceX(g-2,g0) = 317
    c: DistanceY(g-1,g0) = 298.5
FEATURE [Part::Extrusion] Extrude005  label="fan_extrude"
  Base = -> Sketch022
  Dir = (1,0,0)
  DirMode = 2
  FaceMakerClass = Part::FaceMakerBullseye
  LengthFwd = 120
  LengthRev = 0
  Solid = true
  Symmetric = false
FEATURE [TechDraw::DrawSVGTemplate] Template
  EditableTexts = Designed_by_Name=Designed by Name; Drawing_number=Drawing number; FC-Date=Date; FC-SC=Scale; FC-SH=Sheet; FC-Title=Title; Subtitle=Subtitle; Weight=Weight
  Height = 210
  Orientation = 1
  Width = 297
FEATURE [TechDraw::DrawProjGroupItem] ProjItem  label="Front"
  CoarseView = false
  Direction = (0,-1,0)
  Focus = 100
  HardHidden = false
  IsoCount = 0
  IsoHidden = false
  IsoVisible = false
  LockPosition = false
  Perspective = false
  Rotation = 0
  RotationVector = (1,0,0)
  ScaleType = 0
  SeamHidden = false
  SeamVisible = false
  SmoothHidden = false
  SmoothVisible = false
  Source = -> [Body]
  Type = 0
  X = 0
  Y = 0
FEATURE [TechDraw::DrawViewPart] View001  label="3D"
  CoarseView = true
  Direction = (1,1,1)
  Focus = 100
  HardHidden = false
  IsoCount = 0
  IsoHidden = false
  IsoVisible = false
  LockPosition = false
  Perspective = false
  Rotation = 0
  Scale = 0.4
  ScaleType = 0
  SeamHidden = false
  SeamVisible = false
  SmoothHidden = false
  SmoothVisible = false
  Source = -> [Body]
  X = 42.1712
  Y = 10.0412
FEATURE [TechDraw::DrawProjGroupItem] ProjItem002  label="Right"
  CoarseView = false
  Direction = (1,0,0)
  Focus = 100
  HardHidden = false
  IsoCount = 0
  IsoHidden = false
  IsoVisible = false
  LockPosition = true
  Perspective = false
  Rotation = 0
  RotationVector = (0,-1,0)
  Scale = 0.5
  ScaleType = 2
  SeamHidden = false
  SeamVisible = false
  SmoothHidden = false
  SmoothVisible = false
  Source = -> [Body]
  Type = 2
  X = 85.4314
  Y = 0
FEATURE [TechDraw::DrawProjGroupItem] ProjItem005  label="Top"
  CoarseView = false
  Direction = (0,0,1)
  Focus = 100
  HardHidden = false
  IsoCount = 0
  IsoHidden = false
  IsoVisible = false
  LockPosition = true
  Perspective = false
  Rotation = 0
  RotationVector = (1,0,0)
  Scale = 0.5
  ScaleType = 2
  SeamHidden = false
  SeamVisible = false
  SmoothHidden = false
  SmoothVisible = false
  Source = -> [Body]
  Type = 4
  X = 0
  Y = -93.5882
FEATURE [TechDraw::DrawProjGroup] ProjGroup
  Anchor = -> ProjItem
  AutoDistribute = false
  CubeDirs = (6) [(0,0,-1),(0,-1,0),(-1,0,0),(0,1,0),(1,0,0),(0,0,1)]
  CubeRotations = (6) [(1,0,0),(1,0,0),(0,1,0),(-1,0,0),(0,-1,0),(1,0,0)]
  LockPosition = false
  ProjectionType = 0
  Rotation = 0
  Scale = 0.4
  ScaleType = 2
  Source = -> [Body]
  Views = -> [ProjItem,ProjItem002,ProjItem005]
  X = 108.009
  Y = 131.9
  spacingX = 15
  spacingY = 15
FEATURE [TechDraw::DrawViewDimension] Dimension006
  FormatSpec = %.2f
  LockPosition = false
  MeasureType = 1
  References2D = -> [ProjItem005]
  Rotation = 0
  ScaleType = 0
  Type = 1
  X = 25.2669
  Y = -12.5013
FEATURE [TechDraw::DrawViewDimension] Dimension007
  FormatSpec = %.2f
  LockPosition = false
  MeasureType = 1
  References2D = -> [ProjItem005]
  Rotation = 0
  ScaleType = 0
  Type = 2
  X = -21.4733
  Y = -14.1914
FEATURE [TechDraw::DrawViewDimension] Dimension008
  FormatSpec = %.2f
  LockPosition = false
  MeasureType = 1
  References2D = -> [ProjItem005]
  Rotation = 0
  ScaleType = 0
  Type = 1
  X = 21.7868
  Y = 11.3653
FEATURE [TechDraw::DrawViewDimension] Dimension009
  FormatSpec = %.2f
  LockPosition = false
  MeasureType = 1
  References2D = -> [ProjItem]
  Rotation = 0
  ScaleType = 0
  Type = 2
  X = -40.7017
  Y = -5.99637
FEATURE [TechDraw::DrawViewDimension] Dimension010
  FormatSpec = %.2f
  LockPosition = false
  MeasureType = 1
  References2D = -> [ProjItem]
  Rotation = 0
  ScaleType = 0
  Type = 2
  X = -28.0324
  Y = -40.6131
FEATURE [TechDraw::DrawViewDimension] Dimension011
  FormatSpec = %.2f
  LockPosition = false
  MeasureType = 1
  References2D = -> [ProjItem]
  Rotation = 0
  ScaleType = 0
  Type = 1
  X = -17.2769
  Y = -56.1982
FEATURE [TechDraw::DrawViewDimension] Dimension012
  FormatSpec = %.2f
  LockPosition = false
  MeasureType = 1
  References2D = -> [ProjItem]
  Rotation = 0
  ScaleType = 0
  Type = 2
  X = 22.8345
  Y = 11.9908
FEATURE [TechDraw::DrawViewDimension] Dimension013
  FormatSpec = %.2f
  LockPosition = false
  MeasureType = 1
  References2D = -> [ProjItem]
  Rotation = 0
  ScaleType = 0
  Type = 1
  X = 17.3848
  Y = 33.3949
FEATURE [TechDraw::DrawViewDimension] Dimension014
  FormatSpec = %.2f
  LockPosition = false
  MeasureType = 1
  References2D = -> [ProjItem002]
  Rotation = 0
  ScaleType = 0
  Type = 2
  X = -23.4794
  Y = -38.5396
FEATURE [TechDraw::DrawViewDimension] Dimension015
  FormatSpec = %.2f
  LockPosition = false
  MeasureType = 1
  References2D = -> [ProjItem002]
  Rotation = 0
  ScaleType = 0
  Type = 1
  X = -16.1457
  Y = -56.9251
FEATURE [TechDraw::DrawViewDimension] Dimension016
  FormatSpec = %.2f
  LockPosition = false
  MeasureType = 1
  References2D = -> [ProjItem002]
  Rotation = 0
  ScaleType = 0
  Type = 2
  X = 30.7938
  Y = -9.17161
FEATURE [TechDraw::DrawViewDimension] Dimension017
  FormatSpec = %.2f
  LockPosition = false
  MeasureType = 1
  References2D = -> [ProjItem002]
  Rotation = 0
  ScaleType = 0
  Type = 1
  X = 17.7618
  Y = 0.086541
FEATURE [TechDraw::DrawViewDimension] Dimension018
  FormatSpec = %.2f
  LockPosition = false
  MeasureType = 1
  References2D = -> [ProjItem002]
  Rotation = 0
  ScaleType = 0
  Type = 5
  X = 33.8325
  Y = 24.5245
FEATURE [TechDraw::DrawViewAnnotation] Annotation001  label="x4"
  Font = osifont
  LineSpace = 80
  LockPosition = false
  MaxWidth = -1
  Rotation = 0
  ScaleType = 0
  Text = Vertical angle bar
  TextSize = 6
  TextStyle = 0
  X = 44.6785
  Y = 27.152
FEATURE [TechDraw::DrawViewDimension] Dimension019
  FormatSpec = %.2f
  LockPosition = false
  MeasureType = 1
  References2D = -> [ProjItem002]
  Rotation = 0
  ScaleType = 0
  Type = 5
  X = -24.5806
  Y = -22.4054
FEATURE [TechDraw::DrawViewDimension] Dimension020
  FormatSpec = %.2f
  LockPosition = false
  MeasureType = 1
  References2D = -> [ProjItem]
  Rotation = 0
  ScaleType = 0
  Type = 5
  X = 31.2442
  Y = 53.8345
FEATURE [TechDraw::DrawViewDimension] Dimension021
  FormatSpec = %.2f
  LockPosition = false
  MeasureType = 1
  References2D = -> [ProjItem]
  Rotation = 0
  ScaleType = 0
  Type = 5
  X = -25.1114
  Y = -25.1905
FEATURE [TechDraw::DrawPage] Page001  label="test"
  KeepUpdated = true
  ProjectionType = 0
  Template = -> Template
  Views = -> [ProjGroup,View001,Dimension006,Dimension007,Dimension008,Dimension009,Dimension010,Dimension011,Dimension012,Dimension013,Dimension014,Dimension015,Dimension016,Dimension017,Dimension018,Annotation001,Dimension019,Dimension020,Dimension021]
FEATURE [TechDraw::DrawViewPart] View  label="2x side_bottom"
  CoarseView = false
  Direction = (1,-1,0)
  Focus = 100
  HardHidden = false
  IsoCount = 0
  IsoHidden = false
  IsoVisible = false
  LockPosition = false
  Perspective = false
  Rotation = 0
  Scale = 0.25
  ScaleType = 0
  SeamHidden = false
  SeamVisible = false
  SmoothHidden = false
  SmoothVisible = false
  Source = -> [Body001]
  X = 208.295
  Y = 132.312
FEATURE [TechDraw::DrawViewPart] View002  label="open_air_case_frame"
  CoarseView = false
  Direction = (1,-1,1)
  Focus = 100
  HardHidden = false
  IsoCount = 0
  IsoHidden = false
  IsoVisible = false
  LockPosition = false
  Perspective = false
  Rotation = 0
  Scale = 0.15
  ScaleType = 0
  SeamHidden = false
  SeamVisible = false
  SmoothHidden = false
  SmoothVisible = false
  Source = -> [Group]
  X = 70.5448
  Y = 144.974
FEATURE [TechDraw::DrawViewPart] View003  label="2x vertical_back"
  CoarseView = false
  Direction = (1,-1,1)
  Focus = 100
  HardHidden = false
  IsoCount = 0
  IsoHidden = false
  IsoVisible = false
  LockPosition = false
  Perspective = false
  Rotation = 0
  Scale = 0.25
  ScaleType = 0
  SeamHidden = false
  SeamVisible = false
  SmoothHidden = false
  SmoothVisible = false
  Source = -> [Body002]
  X = 262.064
  Y = 159.273
FEATURE [TechDraw::DrawViewPart] View004  label="2x vertical_front"
  CoarseView = false
  Direction = (1,-1,1)
  Focus = 100
  HardHidden = false
  IsoCount = 0
  IsoHidden = false
  IsoVisible = false
  LockPosition = false
  Perspective = false
  Rotation = 0
  Scale = 0.25
  ScaleType = 0
  SeamHidden = false
  SeamVisible = false
  SmoothHidden = false
  SmoothVisible = false
  Source = -> [Body]
  X = 150.243
  Y = 158.621
FEATURE [TechDraw::DrawViewPart] View005  label="2x side_middle"
  CoarseView = false
  Direction = (1,-1,0)
  Focus = 100
  HardHidden = false
  IsoCount = 0
  IsoHidden = false
  IsoVisible = false
  LockPosition = false
  Perspective = false
  Rotation = 0
  Scale = 0.25
  ScaleType = 0
  SeamHidden = false
  SeamVisible = false
  SmoothHidden = false
  SmoothVisible = false
  Source = -> [Body004]
  X = 206.058
  Y = 160.229
FEATURE [TechDraw::DrawViewPart] View006  label="2x bottom_width"
  Caption = for the front and back
  CoarseView = false
  Direction = (1,-1,0)
  Focus = 100
  HardHidden = false
  IsoCount = 0
  IsoHidden = false
  IsoVisible = false
  LockPosition = false
  Perspective = false
  Rotation = 0
  Scale = 0.25
  ScaleType = 0
  SeamHidden = false
  SeamVisible = false
  SmoothHidden = false
  SmoothVisible = false
  Source = -> [Body003]
  X = 77.6674
  Y = 40.0571
FEATURE [TechDraw::DrawViewPart] View007  label="1x top_front"
  CoarseView = false
  Direction = (1,-1,0)
  Focus = 100
  HardHidden = false
  IsoCount = 0
  IsoHidden = false
  IsoVisible = false
  LockPosition = false
  Perspective = false
  Rotation = 0
  Scale = 0.25
  ScaleType = 0
  SeamHidden = false
  SeamVisible = false
  SmoothHidden = false
  SmoothVisible = false
  Source = -> [Body005]
  X = 77.5988
  Y = 66.6919
FEATURE [TechDraw::DrawViewPart] View008  label="1x cards_holder"
  CoarseView = false
  Direction = (1,-1,0)
  Focus = 100
  HardHidden = false
  IsoCount = 0
  IsoHidden = false
  IsoVisible = false
  LockPosition = false
  Perspective = false
  Rotation = 0
  Scale = 0.25
  ScaleType = 0
  SeamHidden = false
  SeamVisible = false
  SmoothHidden = false
  SmoothVisible = false
  Source = -> [Body006]
  X = 215.808
  Y = 75.6647
FEATURE [TechDraw::DrawViewPart] View009  label="1x fans_bar"
  CoarseView = false
  Direction = (1,-1,0)
  Focus = 100
  HardHidden = false
  IsoCount = 0
  IsoHidden = false
  IsoVisible = false
  LockPosition = false
  Perspective = false
  Rotation = 0
  Scale = 0.25
  ScaleType = 0
  SeamHidden = false
  SeamVisible = false
  SmoothHidden = false
  SmoothVisible = false
  Source = -> [Body007]
  X = 215.492
  Y = 94.5246
FEATURE [TechDraw::DrawSVGTemplate] Template001
  EditableTexts = Designed_by_Name=Designed by Name; Drawing_number=Drawing number; FC-Date=Date; FC-SC=Scale; FC-SH=Sheet; FC-Title=Title; Subtitle=Subtitle; Weight=Weight
  Height = 210
  Orientation = 1
  Width = 297
FEATURE [TechDraw::DrawPage] Page  label="test2"
  KeepUpdated = true
  ProjectionType = 0
  Template = -> Template001
  Views = -> [View,View002,View003,View004,View005,View006,View007,View008,View009]
FEATURE [TechDraw::DrawSVGTemplate] Template002
  Height = 297
  Orientation = 0
  Width = 210
FEATURE [TechDraw::DrawViewImage] Image
  Height = 11690
  ImageFile = <userpath>/Downloads/ikea-ps-armoire-metallique__AA-184475-8_pub.png
  LockPosition = false
  Rotation = 0
  Scale = 2.54
  ScaleType = 2
  Width = 8260
  X = 105.871
  Y = 148.285
FEATURE [TechDraw::DrawViewAnnotation] Annotation002  label="title"
  Font = Open Sans
  LineSpace = 80
  LockPosition = true
  MaxWidth = -1
  Rotation = 0
  ScaleType = 0
  Text = RIGGY
  TextSize = 23
  TextStyle = 1
  X = 61
  Y = 267
FEATURE [TechDraw::DrawViewPart] View010  label="projection"
  CoarseView = false
  Direction = (-0.4,-1,0.6)
  Focus = 100
  HardHidden = false
  IsoCount = 0
  IsoHidden = false
  IsoVisible = false
  LockPosition = true
  Perspective = false
  Rotation = 0
  Scale = 0.25
  ScaleType = 0
  SeamHidden = false
  SeamVisible = false
  SmoothHidden = false
  SmoothVisible = true
  Source = -> [Group]
  X = 106.003
  Y = 136.542
FEATURE [TechDraw::DrawViewAnnotation] Annotation  label="licence"
  Font = Open Sans
  LineSpace = 80
  LockPosition = false
  MaxWidth = -1
  Rotation = 0
  ScaleType = 0
  Text = MIT
  TextSize = 8
  TextStyle = 1
  X = 180.323
  Y = 25.5773
FEATURE [TechDraw::DrawViewAnnotation] Annotation003  label="open_source"
  Font = Open Sans
  LineSpace = 80
  LockPosition = false
  MaxWidth = -1
  Rotation = 0
  ScaleType = 0
  Text = Open Source
  TextSize = 3
  TextStyle = 0
  X = 180.363
  Y = 15.1527
FEATURE [TechDraw::DrawPage] Page002  label="Page001"
  KeepUpdated = true
  ProjectionType = 0
  Template = -> Template002
  Views = -> [Image,Annotation002,View010,Annotation,Annotation003]
FEATURE [TechDraw::DrawSVGTemplate] Template003
  Height = 297
  Orientation = 0
  Width = 210
FEATURE [Part::Feature] Part__Feature  label="rivet"
  shape: bbox 9.42 x 9.42 x 51.8 mm, 18 faces (baked)
FEATURE [TechDraw::DrawViewPart] View012  label="rivets"
  Caption = 28x rivets
  CoarseView = false
  Direction = (0,1,0)
  Focus = 100
  HardHidden = false
  IsoCount = 0
  IsoHidden = false
  IsoVisible = false
  LockPosition = false
  Perspective = false
  Rotation = -68
  Scale = 0.5
  ScaleType = 2
  SeamHidden = false
  SeamVisible = false
  SmoothHidden = false
  SmoothVisible = false
  Source = -> [Part__Feature]
  X = 38.4459
  Y = 276.41
FEATURE [TechDraw::DrawViewPart] View013
  Caption = 2x vertical front
  CoarseView = false
  Direction = (1,-1,1)
  Focus = 100
  HardHidden = false
  IsoCount = 0
  IsoHidden = false
  IsoVisible = false
  LockPosition = false
  Perspective = false
  Rotation = 0
  Scale = 0.3
  ScaleType = 0
  SeamHidden = false
  SeamVisible = false
  SmoothHidden = false
  SmoothVisible = false
  Source = -> [Body]
  X = 32.2652
  Y = 205.943
FEATURE [TechDraw::DrawViewPart] View014
  Caption = 2x side bottom bar
  CoarseView = false
  Direction = (1,-1,1)
  Focus = 100
  HardHidden = false
  IsoCount = 0
  IsoHidden = false
  IsoVisible = false
  LockPosition = false
  Perspective = false
  Rotation = 0
  Scale = 0.3
  ScaleType = 0
  SeamHidden = false
  SeamVisible = false
  SmoothHidden = false
  SmoothVisible = false
  Source = -> [Body001]
  X = 106.779
  Y = 189.185
FEATURE [TechDraw::DrawViewPart] View015
  Caption = 2x vertical back bar
  CoarseView = false
  Direction = (1,-1,1)
  Focus = 100
  HardHidden = false
  IsoCount = 0
  IsoHidden = false
  IsoVisible = false
  LockPosition = false
  Perspective = false
  Rotation = 0
  Scale = 0.3
  ScaleType = 0
  SeamHidden = false
  SeamVisible = false
  SmoothHidden = false
  SmoothVisible = false
  Source = -> [Body002]
  X = 170.499
  Y = 238.81
FEATURE [TechDraw::DrawViewPart] View016
  Caption = 2x side middle bar
  CoarseView = false
  Direction = (1,-1,1)
  Focus = 100
  HardHidden = false
  IsoCount = 0
  IsoHidden = false
  IsoVisible = false
  LockPosition = false
  Perspective = false
  Rotation = 0
  Scale = 0.3
  ScaleType = 0
  SeamHidden = false
  SeamVisible = false
  SmoothHidden = false
  SmoothVisible = false
  Source = -> [Body004]
  X = 92.5317
  Y = 246.666
FEATURE [TechDraw::DrawViewPart] View018
  Caption = 2x bottom bar
  CoarseView = false
  Direction = (1,-1,0.1)
  Focus = 100
  HardHidden = false
  IsoCount = 0
  IsoHidden = false
  IsoVisible = false
  LockPosition = false
  Perspective = false
  Rotation = 0
  Scale = 0.3
  ScaleType = 0
  SeamHidden = false
  SeamVisible = false
  SmoothHidden = false
  SmoothVisible = false
  Source = -> [Body003]
  X = 104.406
  Y = 27.5044
FEATURE [TechDraw::DrawViewPart] View019
  Caption = 1x top front bar
  CoarseView = false
  Direction = (1,-1,0.1)
  Focus = 100
  HardHidden = false
  IsoCount = 0
  IsoHidden = false
  IsoVisible = false
  LockPosition = false
  Perspective = false
  Rotation = 0
  Scale = 0.3
  ScaleType = 0
  SeamHidden = false
  SeamVisible = false
  SmoothHidden = false
  SmoothVisible = false
  Source = -> [Body005]
  X = 103.009
  Y = 61.6296
FEATURE [TechDraw::DrawViewPart] View020
  Caption = 1x cards holder bar
  CoarseView = false
  Direction = (1,-1,0.1)
  Focus = 100
  HardHidden = false
  IsoCount = 0
  IsoHidden = false
  IsoVisible = false
  LockPosition = false
  Perspective = false
  Rotation = 0
  Scale = 0.3
  ScaleType = 0
  SeamHidden = false
  SeamVisible = false
  SmoothHidden = false
  SmoothVisible = false
  Source = -> [Body006]
  X = 106.458
  Y = 134.908
FEATURE [TechDraw::DrawViewPart] View021
  Caption = 1x fans bar
  CoarseView = false
  Direction = (1,-1,0.1)
  Focus = 100
  HardHidden = false
  IsoCount = 0
  IsoHidden = false
  IsoVisible = false
  LockPosition = false
  Perspective = false
  Rotation = 0
  Scale = 0.3
  ScaleType = 0
  SeamHidden = false
  SeamVisible = false
  SmoothHidden = false
  SmoothVisible = false
  Source = -> [Body007]
  X = 107.1
  Y = 99.9497
FEATURE [TechDraw::DrawSVGTemplate] Template004
  Height = 297
  Orientation = 0
  Width = 210
FEATURE [TechDraw::DrawViewPart] View022
  Caption = 2x vertical front
  CoarseView = false
  Direction = (1,1,1)
  Focus = 100
  HardHidden = false
  IsoCount = 0
  IsoHidden = false
  IsoVisible = false
  LockPosition = false
  Perspective = false
  Rotation = 0
  Scale = 0.4
  ScaleType = 0
  SeamHidden = false
  SeamVisible = false
  SmoothHidden = false
  SmoothVisible = false
  Source = -> [Body]
  X = 31
  Y = 227
FEATURE [TechDraw::DrawViewPart] View023
  Caption = 2x vertical back
  CoarseView = false
  Direction = (1,-1,1)
  Focus = 100
  HardHidden = false
  IsoCount = 0
  IsoHidden = false
  IsoVisible = false
  LockPosition = false
  Perspective = false
  Rotation = 0
  Scale = 0.4
  ScaleType = 0
  SeamHidden = false
  SeamVisible = false
  SmoothHidden = false
  SmoothVisible = false
  Source = -> [Body002]
  X = 31
  Y = 83
FEATURE [TechDraw::DrawProjGroupItem] ProjItem006  label="Front001"
  CoarseView = false
  Direction = (0,1,0)
  Focus = 100
  HardHidden = false
  IsoCount = 0
  IsoHidden = false
  IsoVisible = false
  LockPosition = false
  Perspective = false
  Rotation = 0
  RotationVector = (-1,0,0)
  ScaleType = 0
  SeamHidden = false
  SeamVisible = false
  SmoothHidden = false
  SmoothVisible = false
  Source = -> [Body]
  Type = 0
  X = 0
  Y = 0
FEATURE [TechDraw::DrawProjGroupItem] ProjItem007  label="Left"
  CoarseView = false
  Direction = (1,0,0)
  Focus = 100
  HardHidden = false
  IsoCount = 0
  IsoHidden = false
  IsoVisible = false
  LockPosition = true
  Perspective = false
  Rotation = 0
  RotationVector = (0,-1,0)
  ScaleType = 0
  SeamHidden = false
  SeamVisible = false
  SmoothHidden = false
  SmoothVisible = false
  Source = -> [Body]
  Type = 1
  X = 47.4936
  Y = 0
FEATURE [TechDraw::DrawProjGroup] ProjGroup001
  Anchor = -> ProjItem006
  AutoDistribute = true
  CubeDirs = (6) [(0,0,-1),(-1.22465e-16,1,0),(1,1.22465e-16,0),(1.22465e-16,-1,0),(-1,-1.22465e-16,0),(0,0,1)]
  CubeRotations = (6) [(-1,1.22465e-16,0),(-1,1.22465e-16,0),(-1.22465e-16,-1,0),(1,-1.22465e-16,0),(1.22465e-16,1,0),(-1,1.22465e-16,0)]
  LockPosition = false
  ProjectionType = 0
  Rotation = 0
  Scale = 0.35
  ScaleType = 2
  Source = -> [Body]
  Views = -> [ProjItem006,ProjItem007]
  X = 95.4503
  Y = 225.582
  spacingX = 15
  spacingY = 15
FEATURE [TechDraw::DrawViewDimension] Dimension024
  FormatSpec = %.2f
  LockPosition = false
  MeasureType = 1
  References2D = -> [ProjItem006]
  Rotation = 0
  ScaleType = 0
  Type = 2
  X = -40.9468
  Y = -0.827891
FEATURE [TechDraw::DrawViewDimension] Dimension025
  FormatSpec = %.2f
  LockPosition = false
  MeasureType = 1
  References2D = -> [ProjItem006]
  Rotation = 0
  ScaleType = 0
  Type = 1
  X = -15.0101
  Y = 63.3422
FEATURE [TechDraw::DrawViewDimension] Dimension026
  FormatSpec = %.2f
  LockPosition = false
  MeasureType = 1
  References2D = -> [ProjItem006]
  Rotation = 0
  ScaleType = 0
  Type = 5
  X = -24.1774
  Y = 43.8834
FEATURE [TechDraw::DrawViewDimension] Dimension027
  FormatSpec = %.2f
  LockPosition = false
  MeasureType = 1
  References2D = -> [ProjItem006]
  Rotation = 0
  ScaleType = 0
  Type = 5
  X = -25.8079
  Y = -26.0142
FEATURE [TechDraw::DrawViewDimension] Dimension028
  FormatSpec = %.2f
  LockPosition = false
  MeasureType = 1
  References2D = -> [ProjItem007]
  Rotation = 0
  ScaleType = 0
  Type = 5
  X = 31.3266
  Y = 19.6398
FEATURE [TechDraw::DrawViewDimension] Dimension029
  FormatSpec = %.2f
  LockPosition = false
  MeasureType = 1
  References2D = -> [ProjItem007]
  Rotation = 0
  ScaleType = 0
  Type = 5
  X = 30.5587
  Y = -31.0736
FEATURE [TechDraw::DrawViewDimension] Dimension030
  FormatSpec = %.2f
  LockPosition = false
  MeasureType = 1
  References2D = -> [ProjItem006]
  Rotation = 0
  ScaleType = 0
  Type = 0
  X = -22.5043
  Y = -71.6668
FEATURE [TechDraw::DrawViewDimension] Dimension031
  FormatSpec = %.2f
  LockPosition = false
  MeasureType = 1
  References2D = -> [ProjItem006]
  Rotation = 0
  ScaleType = 0
  Type = 0
  X = -13.064
  Y = -62.1451
FEATURE [TechDraw::DrawViewDimension] Dimension032
  FormatSpec = %.2f
  LockPosition = false
  MeasureType = 1
  References2D = -> [ProjItem007]
  Rotation = 0
  ScaleType = 0
  Type = 1
  X = 25.7334
  Y = -59.8648
FEATURE [TechDraw::DrawViewDimension] Dimension033
  FormatSpec = %.2f
  LockPosition = false
  MeasureType = 1
  References2D = -> [ProjItem007]
  Rotation = 0
  ScaleType = 0
  Type = 0
  X = 36.3247
  Y = -67.9467
FEATURE [TechDraw::DrawHatch] Hatch  label="HatchF2"
  DirProjection = (0,0,1)
  HatchPattern = <path>//share/freecad/Mod/TechDraw/Patterns/simple.svg
  Source = -> ProjItem007 [Face2]
FEATURE [TechDraw::DrawHatch] Hatch001  label="Hatch001F2"
  DirProjection = (0,0,1)
  HatchPattern = <path>//share/freecad/Mod/TechDraw/Patterns/simple.svg
  Source = -> ProjItem006 [Face2]
FEATURE [TechDraw::DrawProjGroupItem] ProjItem008  label="Front002"
  CoarseView = false
  Direction = (0,-1,0)
  Focus = 100
  HardHidden = false
  IsoCount = 0
  IsoHidden = false
  IsoVisible = false
  LockPosition = false
  Perspective = false
  Rotation = 0
  RotationVector = (1,0,0)
  ScaleType = 0
  SeamHidden = false
  SeamVisible = false
  SmoothHidden = false
  SmoothVisible = false
  Source = -> [Body002]
  Type = 0
  X = 0
  Y = 0
FEATURE [TechDraw::DrawProjGroupItem] ProjItem009  label="Right001"
  CoarseView = false
  Direction = (1,0,0)
  Focus = 100
  HardHidden = false
  IsoCount = 0
  IsoHidden = false
  IsoVisible = false
  LockPosition = true
  Perspective = false
  Rotation = 0
  RotationVector = (0,-1,0)
  ScaleType = 0
  SeamHidden = false
  SeamVisible = false
  SmoothHidden = false
  SmoothVisible = false
  Source = -> [Body002]
  Type = 2
  X = -48.3433
  Y = 0
FEATURE [TechDraw::DrawProjGroup] ProjGroup002
  Anchor = -> ProjItem008
  AutoDistribute = true
  CubeDirs = (1) [(0,0,0)]
  CubeRotations = (1) [(0,0,0)]
  LockPosition = false
  ProjectionType = 0
  Rotation = 0
  Scale = 0.35
  ScaleType = 2
  Source = -> [Body002]
  Views = -> [ProjItem008,ProjItem009]
  X = 144.882
  Y = 80.4181
  spacingX = 15
  spacingY = 15
FEATURE [TechDraw::DrawHatch] Hatch002  label="Hatch002F2"
  DirProjection = (0,0,1)
  HatchPattern = <path>//share/freecad/Mod/TechDraw/Patterns/simple.svg
  Source = -> ProjItem008 [Face2]
FEATURE [TechDraw::DrawHatch] Hatch003  label="Hatch003F2"
  DirProjection = (0,0,1)
  HatchPattern = <path>//share/freecad/Mod/TechDraw/Patterns/simple.svg
  Source = -> ProjItem009 [Face2]
FEATURE [TechDraw::DrawViewDimension] Dimension034
  FormatSpec = %.2f
  LockPosition = false
  MeasureType = 1
  References2D = -> [ProjItem007]
  Rotation = 0
  ScaleType = 0
  Type = 1
  X = 17.604
  Y = 63.2059
FEATURE [TechDraw::DrawViewDimension] Dimension035
  FormatSpec = %.2f
  LockPosition = false
  MeasureType = 1
  References2D = -> [ProjItem009]
  Rotation = 0
  ScaleType = 0
  Type = 1
  X = -10.7742
  Y = 61.9069
FEATURE [TechDraw::DrawViewDimension] Dimension036
  FormatSpec = %.2f
  LockPosition = false
  MeasureType = 1
  References2D = -> [ProjItem008]
  Rotation = 0
  ScaleType = 0
  Type = 1
  X = 13.8793
  Y = 62.1957
FEATURE [TechDraw::DrawViewDimension] Dimension037
  FormatSpec = %.2f
  LockPosition = false
  MeasureType = 1
  References2D = -> [ProjItem009]
  Rotation = 0
  ScaleType = 0
  Type = 2
  X = -40.3534
  Y = 1.42644
FEATURE [TechDraw::DrawViewDimension] Dimension038
  FormatSpec = %.2f
  LockPosition = false
  MeasureType = 1
  References2D = -> [ProjItem009]
  Rotation = 0
  ScaleType = 0
  Type = 2
  X = -22.38
  Y = -70.3489
FEATURE [TechDraw::DrawViewDimension] Dimension039
  FormatSpec = %.2f
  LockPosition = false
  MeasureType = 1
  References2D = -> [ProjItem009]
  Rotation = 0
  ScaleType = 0
  Type = 1
  X = -11.0439
  Y = -61.0921
FEATURE [TechDraw::DrawViewDimension] Dimension040
  FormatSpec = %.2f
  LockPosition = false
  MeasureType = 1
  References2D = -> [ProjItem009]
  Rotation = 0
  ScaleType = 0
  Type = 5
  X = -23.6503
  Y = -25.0981
FEATURE [TechDraw::DrawViewDimension] Dimension041
  FormatSpec = %.2f
  LockPosition = false
  MeasureType = 1
  References2D = -> [ProjItem008]
  Rotation = 0
  ScaleType = 0
  Type = 5
  X = 31.0877
  Y = -27.0405
FEATURE [TechDraw::DrawViewDimension] Dimension042
  FormatSpec = %.2f
  LockPosition = false
  MeasureType = 1
  References2D = -> [ProjItem008]
  Rotation = 0
  ScaleType = 0
  Type = 1
  X = 16.4611
  Y = -60.4772
FEATURE [TechDraw::DrawViewDimension] Dimension043
  FormatSpec = %.2f
  LockPosition = false
  MeasureType = 1
  References2D = -> [ProjItem008]
  Rotation = 0
  ScaleType = 0
  Type = 2
  X = 25.1041
  Y = -70.0263
FEATURE [TechDraw::DrawViewDimension] Dimension044
  FormatSpec = %.2f
  LockPosition = false
  MeasureType = 1
  References2D = -> [ProjItem008]
  Rotation = 0
  ScaleType = 0
  Type = 5
  X = 31.011
  Y = 52.75
FEATURE [TechDraw::DrawViewDimension] Dimension045
  FormatSpec = %.2f
  LockPosition = false
  MeasureType = 1
  References2D = -> [ProjItem008]
  Rotation = 0
  ScaleType = 0
  Type = 1
  X = 27.9738
  Y = 38.5745
FEATURE [TechDraw::DrawViewDimension] Dimension046
  FormatSpec = %.2f
  LockPosition = false
  MeasureType = 1
  References2D = -> [ProjItem008]
  Rotation = 0
  ScaleType = 0
  Type = 2
  X = 39.3259
  Y = 27.6198
FEATURE [TechDraw::DrawViewDimension] Dimension047
  FormatSpec = %.2f
  LockPosition = false
  MeasureType = 1
  References2D = -> [ProjItem009]
  Rotation = 0
  ScaleType = 0
  Type = 5
  X = -24.6953
  Y = 19.9332
FEATURE [TechDraw::DrawViewDimension] Dimension048
  FormatSpec = %.2f
  LockPosition = false
  MeasureType = 1
  References2D = -> [ProjItem007]
  Rotation = 0
  ScaleType = 0
  Type = 2
  X = 51.394
  Y = -10.2823
FEATURE [TechDraw::DrawViewDimension] Dimension049
  FormatSpec = %.2f
  LockPosition = false
  MeasureType = 1
  References2D = -> [ProjItem007]
  Rotation = 0
  ScaleType = 0
  Type = 1
  X = 43.3747
  Y = 0.045707
FEATURE [TechDraw::DrawViewDimension] Dimension050
  FormatSpec = %.2f
  LockPosition = false
  MeasureType = 1
  References2D = -> [ProjItem006]
  Rotation = 0
  ScaleType = 0
  Type = 2
  X = 22.8204
  Y = 19.6806
FEATURE [TechDraw::DrawViewDimension] Dimension051
  FormatSpec = %.2f
  LockPosition = false
  MeasureType = 1
  References2D = -> [ProjItem006]
  Rotation = 0
  ScaleType = 0
  Type = 1
  X = 15.7777
  Y = 29.9162
FEATURE [TechDraw::DrawViewDimension] Dimension052
  FormatSpec = %.2f
  LockPosition = false
  MeasureType = 1
  References2D = -> [ProjItem009]
  Rotation = 0
  ScaleType = 0
  Type = 2
  X = 22.0785
  Y = -11.3852
FEATURE [TechDraw::DrawViewDimension] Dimension053
  FormatSpec = %.2f
  LockPosition = false
  MeasureType = 1
  References2D = -> [ProjItem009]
  Rotation = 0
  ScaleType = 0
  Type = 1
  X = 15.2429
  Y = -0.882165
FEATURE [TechDraw::DrawViewAnnotation] Annotation004  label="1"
  Font = Open Sans
  LineSpace = 80
  LockPosition = false
  MaxWidth = -1
  Rotation = 0
  ScaleType = 0
  Text = 1
  TextSize = 10
  TextStyle = 1
  X = 13
  Y = 284
FEATURE [TechDraw::DrawViewAnnotation] Annotation005  label="2"
  Font = Open Sans
  LineSpace = 80
  LockPosition = false
  MaxWidth = -1
  Rotation = 0
  ScaleType = 0
  Text = 2
  TextSize = 10
  TextStyle = 1
  X = 13
  Y = 145
FEATURE [TechDraw::DrawPage] Page004  label="Page003"
  KeepUpdated = true
  ProjectionType = 0
  Template = -> Template004
  Views = -> [View022,View023,ProjGroup001,Dimension024,Dimension025,Dimension026,Dimension027,Dimension028,Dimension029,Dimension030,Dimension031,Dimension032,Dimension033,ProjGroup002,Dimension034,Dimension035,Dimension036,Dimension037,Dimension038,Dimension039,Dimension040,Dimension041,Dimension042,Dimension043,Dimension044,Dimension045,Dimension046,Dimension047,Dimension048,Dimension049,Dimension050,+5 more]
FEATURE [App::DocumentObjectGroup] Group003  label="extras"
  Group = -> [Part__Feature,Extrude,Extrude005]
FEATURE [TechDraw::DrawSVGTemplate] Template005
  Height = 297
  Orientation = 0
  Width = 210
FEATURE [TechDraw::DrawSVGTemplate] Template006
  Height = 297
  Orientation = 0
  Width = 210
FEATURE [TechDraw::DrawViewAnnotation] Annotation006  label="3"
  Font = Open Sans
  LineSpace = 80
  LockPosition = false
  MaxWidth = -1
  Rotation = 0
  ScaleType = 0
  Text = 3
  TextSize = 10
  TextStyle = 1
  X = 13
  Y = 284
FEATURE [TechDraw::DrawViewAnnotation] Annotation007  label="4"
  Font = Open Sans
  LineSpace = 80
  LockPosition = false
  MaxWidth = -1
  Rotation = 0
  ScaleType = 0
  Text = 4
  TextSize = 10
  TextStyle = 1
  X = 13
  Y = 145
FEATURE [TechDraw::DrawViewPart] View024
  Caption = 2x bottom side bar
  CoarseView = false
  Direction = (1,0,1)
  Focus = 100
  HardHidden = false
  IsoCount = 0
  IsoHidden = false
  IsoVisible = false
  LockPosition = false
  Perspective = false
  Rotation = 0
  Scale = 0.4
  ScaleType = 2
  SeamHidden = false
  SeamVisible = false
  SmoothHidden = false
  SmoothVisible = false
  Source = -> [Body001]
  X = 105.108
  Y = 138.569
FEATURE [TechDraw::DrawViewPart] View025
  Caption = 2x middle side bar
  CoarseView = false
  Direction = (1,0,-1)
  Focus = 100
  HardHidden = false
  IsoCount = 0
  IsoHidden = false
  IsoVisible = false
  LockPosition = false
  Perspective = false
  Rotation = 0
  Scale = 0.4
  ScaleType = 2
  SeamHidden = false
  SeamVisible = false
  SmoothHidden = false
  SmoothVisible = false
  Source = -> [Body004]
  X = 104.235
  Y = 275.429
FEATURE [TechDraw::DrawProjGroupItem] ProjItem010  label="Front003"
  CoarseView = false
  Direction = (1,0,0)
  Focus = 100
  HardHidden = false
  IsoCount = 0
  IsoHidden = false
  IsoVisible = false
  LockPosition = false
  Perspective = false
  Rotation = 0
  RotationVector = (0,-1,0)
  ScaleType = 0
  SeamHidden = false
  SeamVisible = false
  SmoothHidden = false
  SmoothVisible = false
  Source = -> [Body004]
  Type = 0
  X = 0
  Y = 0
FEATURE [TechDraw::DrawProjGroupItem] ProjItem011  label="Bottom001"
  CoarseView = false
  Direction = (0,0,-1)
  Focus = 100
  HardHidden = false
  IsoCount = 0
  IsoHidden = false
  IsoVisible = false
  LockPosition = true
  Perspective = false
  Rotation = 0
  RotationVector = (0,-1,0)
  ScaleType = 0
  SeamHidden = false
  SeamVisible = false
  SmoothHidden = false
  SmoothVisible = false
  Source = -> [Body004]
  Type = 5
  X = 0
  Y = 33.3099
FEATURE [TechDraw::DrawProjGroup] ProjGroup003
  Anchor = -> ProjItem010
  AutoDistribute = true
  CubeDirs = (6) [(0,0,-1),(1,1.83697e-16,0),(1.83697e-16,-1,0),(-1,-1.83697e-16,0),(-1.83697e-16,1,0),(0,0,1)]
  CubeRotations = (6) [(-1.83697e-16,-1,0),(-1.83697e-16,-1,0),(1,-1.83697e-16,0),(1.83697e-16,1,0),(-1,1.83697e-16,0),(-1.83697e-16,-1,0)]
  LockPosition = false
  ProjectionType = 0
  Rotation = 0
  Scale = 0.35
  ScaleType = 2
  Source = -> [Body004]
  Views = -> [ProjItem010,ProjItem011]
  X = 108.857
  Y = 192.941
  spacingX = 15
  spacingY = 15
FEATURE [TechDraw::DrawProjGroupItem] ProjItem012  label="Front004"
  CoarseView = false
  Direction = (1,0,0)
  Focus = 100
  HardHidden = false
  IsoCount = 0
  IsoHidden = false
  IsoVisible = false
  LockPosition = false
  Perspective = false
  Rotation = 0
  RotationVector = (0,-1,0)
  ScaleType = 0
  SeamHidden = false
  SeamVisible = false
  SmoothHidden = false
  SmoothVisible = false
  Source = -> [Body001]
  Type = 0
  X = 0
  Y = 0
FEATURE [TechDraw::DrawProjGroupItem] ProjItem013  label="Top001"
  CoarseView = false
  Direction = (0,0,1)
  Focus = 100
  HardHidden = false
  IsoCount = 0
  IsoHidden = false
  IsoVisible = false
  LockPosition = true
  Perspective = false
  Rotation = 0
  RotationVector = (0,-1,0)
  ScaleType = 0
  SeamHidden = false
  SeamVisible = false
  SmoothHidden = false
  SmoothVisible = false
  Source = -> [Body001]
  Type = 4
  X = 0
  Y = -43.7296
FEATURE [TechDraw::DrawProjGroup] ProjGroup004
  Anchor = -> ProjItem012
  AutoDistribute = true
  CubeDirs = (6) [(0,0,-1),(1,1.83697e-16,0),(1.83697e-16,-1,0),(-1,-1.83697e-16,0),(-1.83697e-16,1,0),(0,0,1)]
  CubeRotations = (6) [(-1.83697e-16,-1,0),(-1.83697e-16,-1,0),(1,-1.83697e-16,0),(1.83697e-16,1,0),(-1,1.83697e-16,0),(-1.83697e-16,-1,0)]
  LockPosition = false
  ProjectionType = 0
  Rotation = 0
  Scale = 0.35
  ScaleType = 2
  Source = -> [Body001]
  Views = -> [ProjItem012,ProjItem013]
  X = 108.792
  Y = 84.1744
  spacingX = 15
  spacingY = 15
FEATURE [TechDraw::DrawViewDimension] Dimension054
  FormatSpec = %.2f
  LockPosition = false
  MeasureType = 1
  References2D = -> [ProjItem011]
  Rotation = 0
  ScaleType = 0
  Type = 1
  X = -6.82561
  Y = 23.6889
FEATURE [TechDraw::DrawViewDimension] Dimension055
  FormatSpec = %.2f
  LockPosition = false
  MeasureType = 1
  References2D = -> [ProjItem011]
  Rotation = 0
  ScaleType = 0
  Type = 2
  X = -77.29
  Y = 13.7659
FEATURE [TechDraw::DrawViewDimension] Dimension056
  FormatSpec = %.2f
  LockPosition = false
  MeasureType = 1
  References2D = -> [ProjItem010]
  Rotation = 0
  ScaleType = 0
  Type = 2
  X = -78.1981
  Y = 13.4313
FEATURE [TechDraw::DrawViewDimension] Dimension057
  FormatSpec = %.2f
  LockPosition = false
  MeasureType = 1
  References2D = -> [ProjItem011]
  Rotation = 0
  ScaleType = 0
  Type = 1
  X = 67.1612
  Y = -14.2906
FEATURE [TechDraw::DrawViewDimension] Dimension058
  FormatSpec = %.2f
  LockPosition = false
  MeasureType = 1
  References2D = -> [ProjItem011]
  Rotation = 0
  ScaleType = 0
  Type = 2
  X = 74.3244
  Y = -5.86369
FEATURE [TechDraw::DrawViewDimension] Dimension059
  FormatSpec = %.2f
  LockPosition = false
  MeasureType = 1
  References2D = -> [ProjItem011]
  Rotation = 0
  ScaleType = 0
  Type = 5
  X = 17.5404
  Y = 12.3641
FEATURE [TechDraw::DrawViewDimension] Dimension060
  FormatSpec = %.2f
  LockPosition = false
  MeasureType = 1
  References2D = -> [ProjItem010]
  Rotation = 0
  ScaleType = 0
  Type = 5
  X = -23.0996
  Y = 15.7606
FEATURE [TechDraw::DrawViewDimension] Dimension061
  FormatSpec = %.2f
  LockPosition = false
  MeasureType = 1
  References2D = -> [ProjItem010]
  Rotation = 0
  ScaleType = 0
  Type = 5
  X = 26.0272
  Y = -13.0776
FEATURE [TechDraw::DrawViewDimension] Dimension062
  FormatSpec = %.2f
  LockPosition = false
  MeasureType = 1
  References2D = -> [ProjItem010]
  Rotation = 0
  ScaleType = 0
  Type = 1
  X = 64.8979
  Y = -21.1277
FEATURE [TechDraw::DrawViewDimension] Dimension063
  FormatSpec = %.2f
  LockPosition = false
  MeasureType = 1
  References2D = -> [ProjItem010]
  Rotation = 0
  ScaleType = 0
  Type = 2
  X = 72.2702
  Y = -14.1369
FEATURE [TechDraw::DrawViewDimension] Dimension064
  FormatSpec = %.2f
  LockPosition = false
  MeasureType = 1
  References2D = -> [ProjItem010]
  Rotation = 0
  ScaleType = 0
  Type = 2
  X = -34.2311
  Y = -14.4341
FEATURE [TechDraw::DrawViewDimension] Dimension065
  FormatSpec = %.2f
  LockPosition = false
  MeasureType = 1
  References2D = -> [ProjItem010]
  Rotation = 0
  ScaleType = 0
  Type = 1
  X = -41.174
  Y = -22.5029
FEATURE [TechDraw::DrawViewDimension] Dimension066
  FormatSpec = %.2f
  LockPosition = false
  MeasureType = 1
  References2D = -> [ProjItem012]
  Rotation = 0
  ScaleType = 0
  Type = 2
  X = -72.6153
  Y = 10.2097
FEATURE [TechDraw::DrawViewDimension] Dimension067
  FormatSpec = %.2f
  LockPosition = false
  MeasureType = 1
  References2D = -> [ProjItem012]
  Rotation = 0
  ScaleType = 0
  Type = 1
  X = 3.05145
  Y = 28.7754
FEATURE [TechDraw::DrawViewDimension] Dimension068
  FormatSpec = %.2f
  LockPosition = false
  MeasureType = 1
  References2D = -> [ProjItem013]
  Rotation = 0
  ScaleType = 0
  Type = 2
  X = -73.1889
  Y = 12.1025
FEATURE [TechDraw::DrawViewDimension] Dimension069
  FormatSpec = %.2f
  LockPosition = false
  MeasureType = 1
  References2D = -> [ProjItem013]
  Rotation = 0
  ScaleType = 0
  Type = 5
  X = -19.9606
  Y = 14.7295
FEATURE [TechDraw::DrawViewDimension] Dimension070
  FormatSpec = %.2f
  LockPosition = false
  MeasureType = 1
  References2D = -> [ProjItem012]
  Rotation = 0
  ScaleType = 0
  Type = 5
  X = -23.5168
  Y = 18.1022
FEATURE [TechDraw::DrawViewDimension] Dimension071
  FormatSpec = %.2f
  LockPosition = false
  MeasureType = 1
  References2D = -> [ProjItem012]
  Rotation = 0
  ScaleType = 0
  Type = 5
  X = 23.838
  Y = -11.2307
FEATURE [TechDraw::DrawViewDimension] Dimension072
  FormatSpec = %.2f
  LockPosition = false
  MeasureType = 1
  References2D = -> [ProjItem013]
  Rotation = 0
  ScaleType = 0
  Type = 5
  X = 20.1327
  Y = -14.741
FEATURE [TechDraw::DrawViewDimension] Dimension073
  FormatSpec = %.2f
  LockPosition = false
  MeasureType = 1
  References2D = -> [ProjItem013]
  Rotation = 0
  ScaleType = 0
  Type = 1
  X = 69.9648
  Y = -18.9282
FEATURE [TechDraw::DrawViewDimension] Dimension074
  FormatSpec = %.2f
  LockPosition = false
  MeasureType = 1
  References2D = -> [ProjItem013]
  Rotation = 0
  ScaleType = 0
  Type = 2
  X = 79.4547
  Y = -12.3764
FEATURE [TechDraw::DrawViewDimension] Dimension075
  FormatSpec = %.2f
  LockPosition = false
  MeasureType = 1
  References2D = -> [ProjItem012]
  Rotation = 0
  ScaleType = 0
  Type = 1
  X = 67.5465
  Y = -16.6616
FEATURE [TechDraw::DrawViewDimension] Dimension076
  FormatSpec = %.2f
  LockPosition = false
  MeasureType = 1
  References2D = -> [ProjItem012]
  Rotation = 0
  ScaleType = 0
  Type = 2
  X = 74.5096
  Y = -8.98509
FEATURE [TechDraw::DrawViewDimension] Dimension077
  FormatSpec = %.2f
  LockPosition = false
  MeasureType = 1
  References2D = -> [ProjItem012]
  Rotation = 0
  ScaleType = 0
  Type = 2
  X = -36.56
  Y = -11.2078
FEATURE [TechDraw::DrawViewDimension] Dimension078
  FormatSpec = %.2f
  LockPosition = false
  MeasureType = 1
  References2D = -> [ProjItem012]
  Rotation = 0
  ScaleType = 0
  Type = 1
  X = -44.3607
  Y = -18.5267
FEATURE [TechDraw::DrawViewDimension] Dimension079
  FormatSpec = %.2f
  LockPosition = false
  MeasureType = 1
  References2D = -> [ProjItem013]
  Rotation = 0
  ScaleType = 0
  Type = 1
  X = -41.9036
  Y = -19.1688
FEATURE [TechDraw::DrawViewDimension] Dimension080
  FormatSpec = %.2f
  LockPosition = false
  MeasureType = 1
  References2D = -> [ProjItem013]
  Rotation = 0
  ScaleType = 0
  Type = 2
  X = -33.2757
  Y = -11.9766
FEATURE [TechDraw::DrawPage] Page005
  KeepUpdated = true
  ProjectionType = 0
  Template = -> Template005
  Views = -> [Annotation006,Annotation007,View024,View025,ProjGroup003,ProjGroup004,Dimension054,Dimension055,Dimension056,Dimension057,Dimension058,Dimension059,Dimension060,Dimension061,Dimension062,Dimension063,Dimension064,Dimension065,Dimension066,Dimension067,Dimension068,Dimension069,Dimension070,Dimension071,Dimension072,Dimension073,Dimension074,Dimension075,Dimension076,Dimension077,Dimension078,+2 more]
FEATURE [TechDraw::DrawHatch] Hatch004  label="Hatch004F2"
  DirProjection = (0,0,1)
  HatchPattern = <path>//share/freecad/Mod/TechDraw/Patterns/simple.svg
  Source = -> ProjItem011 [Face2]
FEATURE [TechDraw::DrawHatch] Hatch005  label="Hatch005F2"
  DirProjection = (0,0,1)
  HatchPattern = <path>//share/freecad/Mod/TechDraw/Patterns/simple.svg
  Source = -> ProjItem010 [Face2]
FEATURE [TechDraw::DrawHatch] Hatch006  label="Hatch006F2"
  DirProjection = (0,0,1)
  HatchPattern = <path>//share/freecad/Mod/TechDraw/Patterns/simple.svg
  Source = -> ProjItem012 [Face2]
FEATURE [TechDraw::DrawHatch] Hatch007  label="Hatch007F2"
  DirProjection = (0,0,1)
  HatchPattern = <path>//share/freecad/Mod/TechDraw/Patterns/simple.svg
  Source = -> ProjItem013 [Face2]
FEATURE [TechDraw::DrawViewPart] View026
  Caption = 2x full side
  CoarseView = false
  Direction = (1,-1,1)
  Focus = 100
  HardHidden = false
  IsoCount = 0
  IsoHidden = false
  IsoVisible = false
  LockPosition = false
  Perspective = false
  Rotation = 0
  Scale = 0.4
  ScaleType = 0
  SeamHidden = false
  SeamVisible = false
  SmoothHidden = false
  SmoothVisible = false
  Source = -> [Body,Body002,Body001,Body004]
  X = 105.271
  Y = 164.789
FEATURE [TechDraw::DrawViewAnnotation] Annotation008  label="5"
  Font = Open Sans
  LineSpace = 80
  LockPosition = false
  MaxWidth = -1
  Rotation = 0
  ScaleType = 0
  Text = 5
  TextSize = 10
  TextStyle = 1
  X = 13
  Y = 284
FEATURE [TechDraw::DrawPage] Page006
  KeepUpdated = true
  ProjectionType = 0
  Template = -> Template006
  Views = -> [View026,Annotation008]
FEATURE [TechDraw::DrawSVGTemplate] Template007
  Height = 297
  Orientation = 0
  Width = 210
FEATURE [TechDraw::DrawSVGTemplate] Template008
  Height = 297
  Orientation = 0
  Width = 210
FEATURE [TechDraw::DrawSVGTemplate] Template009
  Height = 297
  Orientation = 0
  Width = 210
FEATURE [TechDraw::DrawViewAnnotation] Annotation009  label="6"
  Font = Open Sans
  LineSpace = 80
  LockPosition = false
  MaxWidth = -1
  Rotation = 0
  ScaleType = 0
  Text = 6
  TextSize = 10
  TextStyle = 1
  X = 13
  Y = 284
FEATURE [TechDraw::DrawViewAnnotation] Annotation010  label="7"
  Font = Open Sans
  LineSpace = 80
  LockPosition = false
  MaxWidth = -1
  Rotation = 0
  ScaleType = 0
  Text = 7
  TextSize = 10
  TextStyle = 1
  X = 13
  Y = 145
FEATURE [TechDraw::DrawViewAnnotation] Annotation011  label="8"
  Font = Open Sans
  LineSpace = 80
  LockPosition = false
  MaxWidth = -1
  Rotation = 0
  ScaleType = 0
  Text = 8
  TextSize = 10
  TextStyle = 1
  X = 13
  Y = 284
FEATURE [TechDraw::DrawViewAnnotation] Annotation012  label="9"
  Font = Open Sans
  LineSpace = 80
  LockPosition = false
  MaxWidth = -1
  Rotation = 0
  ScaleType = 0
  Text = 9
  TextSize = 10
  TextStyle = 1
  X = 13
  Y = 145
FEATURE [TechDraw::DrawPage] Page008
  KeepUpdated = true
  ProjectionType = 0
  Template = -> Template008
  Views = -> [Annotation011,Annotation012]
FEATURE [TechDraw::DrawViewAnnotation] Annotation013  label="10"
  Font = Open Sans
  LineSpace = 80
  LockPosition = false
  MaxWidth = -1
  Rotation = 0
  ScaleType = 0
  Text = 10
  TextSize = 10
  TextStyle = 1
  X = 13
  Y = 284
FEATURE [TechDraw::DrawPage] Page009
  KeepUpdated = true
  ProjectionType = 0
  Template = -> Template009
  Views = -> [Annotation013]
FEATURE [TechDraw::DrawViewPart] View027
  Caption = 2x bottom bar
  CoarseView = false
  Direction = (0.25,1,1)
  Focus = 100
  HardHidden = false
  IsoCount = 0
  IsoHidden = false
  IsoVisible = false
  LockPosition = false
  Perspective = false
  Rotation = 0
  Scale = 0.3
  ScaleType = 2
  SeamHidden = false
  SeamVisible = false
  SmoothHidden = false
  SmoothVisible = false
  Source = -> [Body003]
  X = 102.281
  Y = 271.097
FEATURE [TechDraw::DrawProjGroupItem] ProjItem014  label="Front005"
  CoarseView = false
  Direction = (0,1,0)
  Focus = 100
  HardHidden = false
  IsoCount = 0
  IsoHidden = false
  IsoVisible = false
  LockPosition = false
  Perspective = false
  Rotation = 0
  RotationVector = (-1,0,0)
  ScaleType = 0
  SeamHidden = false
  SeamVisible = false
  SmoothHidden = false
  SmoothVisible = false
  Source = -> [Body003]
  Type = 0
  X = 0
  Y = 0
FEATURE [TechDraw::DrawProjGroupItem] ProjItem015  label="Top002"
  CoarseView = false
  Direction = (0,0,1)
  Focus = 100
  HardHidden = false
  IsoCount = 0
  IsoHidden = false
  IsoVisible = false
  LockPosition = false
  Perspective = false
  Rotation = 0
  RotationVector = (-1,0,0)
  ScaleType = 0
  SeamHidden = false
  SeamVisible = false
  SmoothHidden = false
  SmoothVisible = false
  Source = -> [Body003]
  Type = 4
  X = 0
  Y = -20.4
FEATURE [TechDraw::DrawProjGroup] ProjGroup005
  Anchor = -> ProjItem014
  AutoDistribute = true
  CubeDirs = (6) [(0,0,-1),(-1.22465e-16,1,0),(1,1.22465e-16,0),(1.22465e-16,-1,0),(-1,-1.22465e-16,0),(0,0,1)]
  CubeRotations = (6) [(-1,1.22465e-16,0),(-1,1.22465e-16,0),(-1.22465e-16,-1,0),(1,-1.22465e-16,0),(1.22465e-16,1,0),(-1,1.22465e-16,0)]
  LockPosition = false
  ProjectionType = 0
  Rotation = 0
  Scale = 0.27
  ScaleType = 2
  Source = -> [Body003]
  Views = -> [ProjItem014,ProjItem015]
  X = 103.267
  Y = 222.093
  spacingX = 15
  spacingY = 15
FEATURE [TechDraw::DrawViewDimension] Dimension081
  FormatSpec = %.2f
  LockPosition = false
  MeasureType = 1
  References2D = -> [ProjItem014]
  Rotation = 0
  ScaleType = 0
  Type = 5
  X = 49.8905
  Y = -10.1469
FEATURE [TechDraw::DrawViewDimension] Dimension082
  FormatSpec = %.2f
  LockPosition = false
  MeasureType = 1
  References2D = -> [ProjItem014]
  Rotation = 0
  ScaleType = 0
  Type = 5
  X = -53.6817
  Y = -10.9074
FEATURE [TechDraw::DrawViewDimension] Dimension083
  FormatSpec = %.2f
  LockPosition = false
  MeasureType = 1
  References2D = -> [ProjItem015]
  Rotation = 0
  ScaleType = 0
  Type = 5
  X = -56.1279
  Y = 12.8019
FEATURE [TechDraw::DrawViewDimension] Dimension084
  FormatSpec = %.2f
  LockPosition = false
  MeasureType = 1
  References2D = -> [ProjItem015]
  Rotation = 0
  ScaleType = 0
  Type = 5
  X = 55.3546
  Y = 12.2375
FEATURE [TechDraw::DrawViewDimension] Dimension085
  FormatSpec = %.2f
  LockPosition = false
  MeasureType = 1
  References2D = -> [ProjItem014]
  Rotation = 0
  ScaleType = 0
  Type = 2
  X = -95.3505
  Y = 12.231
FEATURE [TechDraw::DrawViewDimension] Dimension086
  FormatSpec = %.2f
  LockPosition = false
  MeasureType = 1
  References2D = -> [ProjItem015]
  Rotation = 0
  ScaleType = 0
  Type = 2
  X = -95.5865
  Y = 13.0584
FEATURE [TechDraw::DrawViewDimension] Dimension087
  FormatSpec = %.2f
  LockPosition = false
  MeasureType = 1
  References2D = -> [ProjItem014]
  Rotation = 0
  ScaleType = 0
  Type = 1
  X = 31.4735
  Y = 24.621
FEATURE [TechDraw::DrawViewDimension] Dimension088
  FormatSpec = %.2f
  LockPosition = false
  MeasureType = 1
  References2D = -> [ProjItem015]
  Rotation = 0
  ScaleType = 0
  Type = 2
  X = -68.75
  Y = -12.0976
FEATURE [TechDraw::DrawViewDimension] Dimension089
  FormatSpec = %.2f
  LockPosition = false
  MeasureType = 1
  References2D = -> [ProjItem015]
  Rotation = 0
  ScaleType = 0
  Type = 1
  X = -77.2716
  Y = -18.563
FEATURE [TechDraw::DrawViewDimension] Dimension090
  FormatSpec = %.2f
  LockPosition = false
  MeasureType = 1
  References2D = -> [ProjItem015]
  Rotation = 0
  ScaleType = 0
  Type = 1
  X = 92.2752
  Y = -16.2517
FEATURE [TechDraw::DrawViewDimension] Dimension091
  FormatSpec = %.2f
  LockPosition = false
  MeasureType = 1
  References2D = -> [ProjItem015]
  Rotation = 0
  ScaleType = 0
  Type = 2
  X = 99.5539
  Y = -9.37358
FEATURE [TechDraw::DrawViewDimension] Dimension092
  FormatSpec = %.2f
  LockPosition = false
  MeasureType = 1
  References2D = -> [ProjItem014]
  Rotation = 0
  ScaleType = 0
  Type = 1
  X = 96.2051
  Y = -9.65375
FEATURE [TechDraw::DrawViewDimension] Dimension093
  FormatSpec = %.2f
  LockPosition = false
  MeasureType = 1
  References2D = -> [ProjItem014]
  Rotation = 0
  ScaleType = 0
  Type = 2
  X = 99.8916
  Y = 16.2217
FEATURE [TechDraw::DrawViewDimension] Dimension094
  FormatSpec = %.2f
  LockPosition = false
  MeasureType = 1
  References2D = -> [ProjItem014]
  Rotation = 0
  ScaleType = 0
  Type = 2
  X = -62.002
  Y = 14.8423
FEATURE [TechDraw::DrawViewDimension] Dimension095
  FormatSpec = %.2f
  LockPosition = false
  MeasureType = 1
  References2D = -> [ProjItem014]
  Rotation = 0
  ScaleType = 0
  Type = 1
  X = -67.8276
  Y = 8.41916
FEATURE [TechDraw::DrawPage] Page007
  KeepUpdated = true
  ProjectionType = 0
  Template = -> Template007
  Views = -> [Annotation009,Annotation010,View027,ProjGroup005,Dimension081,Dimension082,Dimension083,Dimension084,Dimension085,Dimension086,Dimension087,Dimension088,Dimension089,Dimension090,Dimension091,Dimension092,Dimension093,Dimension094,Dimension095]
FEATURE [TechDraw::DrawViewSymbol] Symbol
  LockPosition = false
  Rotation = 0
  ScaleType = 2
  Symbol = <blob: 639716 chars omitted>
  X = 130.113
  Y = 257.431
FEATURE [TechDraw::DrawPage] Page003  label="Page002"
  KeepUpdated = true
  ProjectionType = 0
  Template = -> Template003
  Views = -> [View012,View013,View014,View015,View016,View018,View019,View020,View021,Symbol]
FEATURE [App::DocumentObjectGroup] Group004  label="manual"
  Group = -> [Page002,Page003,Page004,Page005,Page006,Page007,Page008,Page009]
note: 8 file-system paths scrubbed to <path> (originals preserved in the JSON sidecar)
